# Revit family: Elite_Sliding_Window_XX_Standard
name_source: partatom
category: Windows
revit_build: Autodesk Revit 2014 (Build: 20130308_1515(x64)
units: mm (PartAtom-declared; Revit-internal decimal feet)

## types (108) — shared parameters
Centered In Wall = Yes
Custom Sash Width Left = 600 mm
Default Sill Height = 800 mm
Description = Sliding window, XX
Equal Sash Width = Yes
Frame Thickness = 70 mm
Limit Sash Height Max = 1800 mm  [stored 5.90551 ft]
Limit Sash Height Min = 300 mm
Limit Sash Width Max = 1500 mm  [stored 4.92126 ft]
Limit Sash Width Min = 300 mm
Limit Window Height Max = 1883 mm
Limit Window Height Min = 383 mm  [stored 1.25656 ft]
Limit Window Width Min = 594 mm
Manufacturer = Crealco
Model = Elite
Rough Width = 3 mm  [stored 0.00984252 ft]
Sash Frame Seal = 3 mm  [stored 0.00984252 ft]
Sash Side Spacing = 1 mm  [stored 0.00328084 ft]
URL = http://www.crealco.co.za
Wall Closure = By host
zero-valued in all types: Custom Frame Offset From Exterior

## per-type parameters (varying)
- Elite-0906XX-1000Pa: Area Left Sash Glazing=0.16 m²; Area Right Sash Glazing=0.16 m²; Clearvue SHGC Value=0.456; Clearvue U Value=7.11; Custom Windload=1000 mm  [stored 3.28084 ft]; Custom Window Height=590 mm  [stored 1.9357 ft]; Custom Window Width=890 mm  [stored 2.91995 ft]; Energy Advantage SHGC Value=0.412; Energy Advantage U Value=6.21; Height=590 mm  [stored 1.9357 ft]; Inside Heavy Duty Interlocker=No; Interlocker Configuration=0 mm  [stored 0 ft]; Intruderprufe LowE SHGC Value=0.433; Intruderprufe LowE U Value=6.99; Intruderprufe SHGC Value=0.349; Intruderprufe U Value=7.27; Limit Sash Width Left Max=596 mm; Limit Sash Width Left Min=300 mm; Limit Window Width Max=2994 mm; Max Pane Area=0.16 m²; Outside Heavy Duty Interlocker=No; Sash Height=507 mm; Sash Width Left=448 mm; Sash Width Right=448 mm; Standard Interlocker=Yes; Width=890 mm  [stored 2.91995 ft]; Windload Design=1000 mm  [stored 3.28084 ft]
- Elite-1206XX-1000Pa: Area Left Sash Glazing=0.22 m²; Area Right Sash Glazing=0.22 m²; Clearvue SHGC Value=0.49; Clearvue U Value=7; Custom Windload=1000 mm  [stored 3.28084 ft]; Custom Window Height=590 mm  [stored 1.9357 ft]; Custom Window Width=1190 mm  [stored 3.9042 ft]; Energy Advantage SHGC Value=0.442; Energy Advantage U Value=5.95; Height=590 mm  [stored 1.9357 ft]; Inside Heavy Duty Interlocker=No; Interlocker Configuration=0 mm  [stored 0 ft]; Intruderprufe LowE SHGC Value=0.413; Intruderprufe LowE U Value=5.73; Intruderprufe SHGC Value=0.466; Intruderprufe U Value=6.88; Limit Sash Width Left Max=896 mm; Limit Sash Width Left Min=300 mm; Limit Window Width Max=2994 mm; Max Pane Area=0.22 m²; Outside Heavy Duty Interlocker=No; Sash Height=507 mm; Sash Width Left=598 mm; Sash Width Right=598 mm; Standard Interlocker=Yes; Width=1190 mm  [stored 3.9042 ft]; Windload Design=1000 mm  [stored 3.28084 ft]
- Elite-1506XX-1000Pa: Area Left Sash Glazing=0.28 m²; Area Right Sash Glazing=0.28 m²; Clearvue SHGC Value=0.511; Clearvue U Value=6.93; Custom Windload=1000 mm  [stored 3.28084 ft]; Custom Window Height=590 mm  [stored 1.9357 ft]; Custom Window Width=1490 mm  [stored 4.88845 ft]; Energy Advantage SHGC Value=0.46; Energy Advantage U Value=5.8; Height=590 mm  [stored 1.9357 ft]; Inside Heavy Duty Interlocker=No; Interlocker Configuration=0 mm  [stored 0 ft]; Intruderprufe LowE SHGC Value=0.429; Intruderprufe LowE U Value=5.61; Intruderprufe SHGC Value=0.485; Intruderprufe U Value=6.81; Limit Sash Width Left Max=1196 mm; Limit Sash Width Left Min=300 mm; Limit Window Width Max=2994 mm; Max Pane Area=0.28 m²; Outside Heavy Duty Interlocker=No; Sash Height=507 mm; Sash Width Left=748 mm; Sash Width Right=748 mm; Standard Interlocker=Yes; Width=1490 mm  [stored 4.88845 ft]; Windload Design=1000 mm  [stored 3.28084 ft]
- Elite-1806XX-1000Pa: Area Left Sash Glazing=0.35 m²; Area Right Sash Glazing=0.35 m²; Clearvue SHGC Value=0.524; Clearvue U Value=6.88; Custom Windload=1000 mm  [stored 3.28084 ft]; Custom Window Height=590 mm  [stored 1.9357 ft]; Custom Window Width=1790 mm  [stored 5.8727 ft]; Energy Advantage SHGC Value=0.472; Energy Advantage U Value=5.7; Height=590 mm  [stored 1.9357 ft]; Inside Heavy Duty Interlocker=No; Interlocker Configuration=0 mm  [stored 0 ft]; Intruderprufe LowE SHGC Value=0.44; Intruderprufe LowE U Value=5.52; Intruderprufe SHGC Value=0.498; Intruderprufe U Value=6.76; Limit Sash Width Left Max=1496 mm; Limit Sash Width Left Min=300 mm; Limit Window Width Max=2994 mm; Max Pane Area=0.35 m²; Outside Heavy Duty Interlocker=No; Sash Height=507 mm; Sash Width Left=898 mm; Sash Width Right=898 mm; Standard Interlocker=Yes; Width=1790 mm  [stored 5.8727 ft]; Windload Design=1000 mm  [stored 3.28084 ft]
- Elite-2106XX-1000Pa: Area Left Sash Glazing=0.41 m²; Area Right Sash Glazing=0.41 m²; Clearvue SHGC Value=0.534; Clearvue U Value=6.85; Custom Windload=1000 mm  [stored 3.28084 ft]; Custom Window Height=590 mm  [stored 1.9357 ft]; Custom Window Width=2090 mm  [stored 6.85696 ft]; Energy Advantage SHGC Value=0.48; Energy Advantage U Value=5.63; Height=590 mm  [stored 1.9357 ft]; Inside Heavy Duty Interlocker=No; Interlocker Configuration=0 mm  [stored 0 ft]; Intruderprufe LowE SHGC Value=0.448; Intruderprufe LowE U Value=5.46; Intruderprufe SHGC Value=0.507; Intruderprufe U Value=6.763; Limit Sash Width Left Max=1500 mm  [stored 4.92126 ft]; Limit Sash Width Left Min=596 mm; Limit Window Width Max=2994 mm; Max Pane Area=0.41 m²; Outside Heavy Duty Interlocker=No; Sash Height=507 mm; Sash Width Left=1048 mm; Sash Width Right=1048 mm; Standard Interlocker=Yes; Width=2090 mm  [stored 6.85696 ft]; Windload Design=1000 mm  [stored 3.28084 ft]
- Elite-2406XX-1000Pa: Area Left Sash Glazing=0.47 m²; Area Right Sash Glazing=0.47 m²; Clearvue SHGC Value=0.541; Clearvue U Value=6.82; Custom Windload=1000 mm  [stored 3.28084 ft]; Custom Window Height=590 mm  [stored 1.9357 ft]; Custom Window Width=2390 mm  [stored 7.84121 ft]; Energy Advantage SHGC Value=0.487; Energy Advantage U Value=5.58; Height=590 mm  [stored 1.9357 ft]; Inside Heavy Duty Interlocker=No; Interlocker Configuration=0 mm  [stored 0 ft]; Intruderprufe LowE SHGC Value=0.454; Intruderprufe LowE U Value=5.42; Intruderprufe SHGC Value=0.514; Intruderprufe U Value=6.7; Limit Sash Width Left Max=1500 mm  [stored 4.92126 ft]; Limit Sash Width Left Min=896 mm; Limit Window Width Max=2994 mm; Max Pane Area=0.47 m²; Outside Heavy Duty Interlocker=No; Sash Height=507 mm; Sash Width Left=1198 mm; Sash Width Right=1198 mm; Standard Interlocker=Yes; Width=2390 mm  [stored 7.84121 ft]; Windload Design=1000 mm  [stored 3.28084 ft]
- Elite-2706XX-1000Pa: Area Left Sash Glazing=0.53 m²; Area Right Sash Glazing=0.53 m²; Clearvue SHGC Value=0.547; Clearvue U Value=6.8; Custom Windload=1000 mm  [stored 3.28084 ft]; Custom Window Height=590 mm  [stored 1.9357 ft]; Custom Window Width=2690 mm; Energy Advantage SHGC Value=0.492; Energy Advantage U Value=5.54; Height=590 mm  [stored 1.9357 ft]; Inside Heavy Duty Interlocker=No; Interlocker Configuration=0 mm  [stored 0 ft]; Intruderprufe LowE SHGC Value=0.414; Intruderprufe LowE U Value=6.68; Intruderprufe SHGC Value=0.519; Intruderprufe U Value=6.69; Limit Sash Width Left Max=1500 mm  [stored 4.92126 ft]; Limit Sash Width Left Min=1196 mm; Limit Window Width Max=2994 mm; Max Pane Area=0.53 m²; Outside Heavy Duty Interlocker=No; Sash Height=507 mm; Sash Width Left=1348 mm; Sash Width Right=1348 mm; Standard Interlocker=Yes; Width=2690 mm; Windload Design=1000 mm  [stored 3.28084 ft]
- Elite-3006XX-1000Pa: Area Left Sash Glazing=0.6 m²; Area Right Sash Glazing=0.6 m²; Clearvue SHGC Value=0.551; Clearvue U Value=6.79; Custom Windload=1000 mm  [stored 3.28084 ft]; Custom Window Height=590 mm  [stored 1.9357 ft]; Custom Window Width=2990 mm; Energy Advantage SHGC Value=0.495; Energy Advantage U Value=5.5; Height=590 mm  [stored 1.9357 ft]; Inside Heavy Duty Interlocker=No; Interlocker Configuration=0 mm  [stored 0 ft]; Intruderprufe LowE SHGC Value=0.462; Intruderprufe LowE U Value=5.36; Intruderprufe SHGC Value=0.524; Intruderprufe U Value=6.67; Limit Sash Width Left Max=1500 mm  [stored 4.92126 ft]; Limit Sash Width Left Min=1496 mm; Limit Window Width Max=2994 mm; Max Pane Area=0.6 m²; Outside Heavy Duty Interlocker=No; Sash Height=507 mm; Sash Width Left=1498 mm; Sash Width Right=1498 mm; Standard Interlocker=Yes; Width=2990 mm; Windload Design=1000 mm  [stored 3.28084 ft]
- Elite-0909XX-1000Pa: Area Left Sash Glazing=0.28 m²; Area Right Sash Glazing=0.28 m²; Clearvue SHGC Value=0.521; Clearvue U Value=6.96; Custom Windload=1000 mm  [stored 3.28084 ft]; Custom Window Height=890 mm  [stored 2.91995 ft]; Custom Window Width=890 mm  [stored 2.91995 ft]; Energy Advantage SHGC Value=0.47; Energy Advantage U Value=5.88; Height=890 mm  [stored 2.91995 ft]; Inside Heavy Duty Interlocker=No; Interlocker Configuration=0 mm  [stored 0 ft]; Intruderprufe LowE SHGC Value=0.438; Intruderprufe LowE U Value=5.62; Intruderprufe SHGC Value=0.494; Intruderprufe U Value=6.84; Limit Sash Width Left Max=596 mm; Limit Sash Width Left Min=300 mm; Limit Window Width Max=2994 mm; Max Pane Area=0.28 m²; Outside Heavy Duty Interlocker=No; Sash Height=807 mm  [stored 2.64764 ft]; Sash Width Left=448 mm; Sash Width Right=448 mm; Standard Interlocker=Yes; Width=890 mm  [stored 2.91995 ft]; Windload Design=1000 mm  [stored 3.28084 ft]
- Elite-1209XX-1000Pa: Area Left Sash Glazing=0.38 m²; Area Right Sash Glazing=0.38 m²; Clearvue SHGC Value=0.561; Clearvue U Value=6.82; Custom Windload=1000 mm  [stored 3.28084 ft]; Custom Window Height=890 mm  [stored 2.91995 ft]; Custom Window Width=1190 mm  [stored 3.9042 ft]; Energy Advantage SHGC Value=0.504; Energy Advantage U Value=5.58; Height=890 mm  [stored 2.91995 ft]; Inside Heavy Duty Interlocker=No; Interlocker Configuration=0 mm  [stored 0 ft]; Intruderprufe LowE SHGC Value=0.47; Intruderprufe LowE U Value=5.36; Intruderprufe SHGC Value=0.532; Intruderprufe U Value=6.7; Limit Sash Width Left Max=896 mm; Limit Sash Width Left Min=300 mm; Limit Window Width Max=2994 mm; Max Pane Area=0.38 m²; Outside Heavy Duty Interlocker=No; Sash Height=807 mm  [stored 2.64764 ft]; Sash Width Left=598 mm; Sash Width Right=598 mm; Standard Interlocker=Yes; Width=1190 mm  [stored 3.9042 ft]; Windload Design=1000 mm  [stored 3.28084 ft]
- Elite-1509XX-1000Pa: Area Left Sash Glazing=0.49 m²; Area Right Sash Glazing=0.49 m²; Clearvue SHGC Value=0.584; Clearvue U Value=6.73; Custom Windload=1000 mm  [stored 3.28084 ft]; Custom Window Height=890 mm  [stored 2.91995 ft]; Custom Window Width=1490 mm  [stored 4.88845 ft]; Energy Advantage SHGC Value=0.525; Energy Advantage U Value=5.41; Height=890 mm  [stored 2.91995 ft]; Inside Heavy Duty Interlocker=No; Interlocker Configuration=0 mm  [stored 0 ft]; Intruderprufe LowE SHGC Value=0.489; Intruderprufe LowE U Value=5.21; Intruderprufe SHGC Value=0.55; Intruderprufe U Value=6.61; Limit Sash Width Left Max=1196 mm; Limit Sash Width Left Min=300 mm; Limit Window Width Max=2994 mm; Max Pane Area=0.49 m²; Outside Heavy Duty Interlocker=No; Sash Height=807 mm  [stored 2.64764 ft]; Sash Width Left=748 mm; Sash Width Right=748 mm; Standard Interlocker=Yes; Width=1490 mm  [stored 4.88845 ft]; Windload Design=1000 mm  [stored 3.28084 ft]
- Elite-1809XX-1000Pa: Area Left Sash Glazing=0.6 m²; Area Right Sash Glazing=0.6 m²; Clearvue SHGC Value=2.6; Clearvue U Value=6.68; Custom Windload=1000 mm  [stored 3.28084 ft]; Custom Window Height=890 mm  [stored 2.91995 ft]; Custom Window Width=1790 mm  [stored 5.8727 ft]; Energy Advantage SHGC Value=0.539; Energy Advantage U Value=5.29; Height=890 mm  [stored 2.91995 ft]; Inside Heavy Duty Interlocker=No; Interlocker Configuration=0 mm  [stored 0 ft]; Intruderprufe LowE SHGC Value=0.502; Intruderprufe LowE U Value=5.11; Intruderprufe SHGC Value=0.57; Intruderprufe U Value=6.55; Limit Sash Width Left Max=1496 mm; Limit Sash Width Left Min=300 mm; Limit Window Width Max=2994 mm; Max Pane Area=0.6 m²; Outside Heavy Duty Interlocker=No; Sash Height=807 mm  [stored 2.64764 ft]; Sash Width Left=898 mm; Sash Width Right=898 mm; Standard Interlocker=Yes; Width=1790 mm  [stored 5.8727 ft]; Windload Design=1000 mm  [stored 3.28084 ft]
- Elite-2109XX-1000Pa: Area Left Sash Glazing=0.7 m²; Area Right Sash Glazing=0.7 m²; Clearvue SHGC Value=0.611; Clearvue U Value=6.64; Custom Windload=1000 mm  [stored 3.28084 ft]; Custom Window Height=890 mm  [stored 2.91995 ft]; Custom Window Width=2090 mm  [stored 6.85696 ft]; Energy Advantage SHGC Value=0.549; Energy Advantage U Value=5.2; Height=890 mm  [stored 2.91995 ft]; Inside Heavy Duty Interlocker=No; Interlocker Configuration=0 mm  [stored 0 ft]; Intruderprufe LowE SHGC Value=0.511; Intruderprufe LowE U Value=5.04; Intruderprufe SHGC Value=0.58; Intruderprufe U Value=6.54; Limit Sash Width Left Max=1500 mm  [stored 4.92126 ft]; Limit Sash Width Left Min=596 mm; Limit Window Width Max=2994 mm; Max Pane Area=0.7 m²; Outside Heavy Duty Interlocker=No; Sash Height=807 mm  [stored 2.64764 ft]; Sash Width Left=1048 mm; Sash Width Right=1048 mm; Standard Interlocker=Yes; Width=2090 mm  [stored 6.85696 ft]; Windload Design=1000 mm  [stored 3.28084 ft]
- Elite-2409XX-1000Pa: Area Left Sash Glazing=0.81 m²; Area Right Sash Glazing=0.81 m²; Clearvue SHGC Value=0.62; Clearvue U Value=6.6; Custom Windload=1000 mm  [stored 3.28084 ft]; Custom Window Height=890 mm  [stored 2.91995 ft]; Custom Window Width=2390 mm  [stored 7.84121 ft]; Energy Advantage SHGC Value=0.556; Energy Advantage U Value=5.14; Height=890 mm  [stored 2.91995 ft]; Inside Heavy Duty Interlocker=No; Interlocker Configuration=0 mm  [stored 0 ft]; Intruderprufe LowE SHGC Value=0.518; Intruderprufe LowE U Value=4.99; Intruderprufe SHGC Value=0.588; Intruderprufe U Value=6.48; Limit Sash Width Left Max=1500 mm  [stored 4.92126 ft]; Limit Sash Width Left Min=896 mm; Limit Window Width Max=2994 mm; Max Pane Area=0.81 m²; Outside Heavy Duty Interlocker=No; Sash Height=807 mm  [stored 2.64764 ft]; Sash Width Left=1198 mm; Sash Width Right=1198 mm; Standard Interlocker=Yes; Width=2390 mm  [stored 7.84121 ft]; Windload Design=1000 mm  [stored 3.28084 ft]
- Elite-2709XX-1000Pa: Area Left Sash Glazing=0.92 m²; Area Right Sash Glazing=0.92 m²; Clearvue SHGC Value=0.626; Clearvue U Value=6.58; Custom Windload=1000 mm  [stored 3.28084 ft]; Custom Window Height=890 mm  [stored 2.91995 ft]; Custom Window Width=2690 mm; Energy Advantage SHGC Value=0.562; Energy Advantage U Value=5.09; Height=890 mm  [stored 2.91995 ft]; Inside Heavy Duty Interlocker=No; Interlocker Configuration=0 mm  [stored 0 ft]; Intruderprufe LowE SHGC Value=0.523; Intruderprufe LowE U Value=4.94; Intruderprufe SHGC Value=0.595; Intruderprufe U Value=6.46; Limit Sash Width Left Max=1500 mm  [stored 4.92126 ft]; Limit Sash Width Left Min=1196 mm; Limit Window Width Max=2994 mm; Max Pane Area=0.92 m²; Outside Heavy Duty Interlocker=No; Sash Height=807 mm  [stored 2.64764 ft]; Sash Width Left=1348 mm; Sash Width Right=1348 mm; Standard Interlocker=Yes; Width=2690 mm; Windload Design=1000 mm  [stored 3.28084 ft]
- Elite-3009XX-1000Pa: Area Left Sash Glazing=1.03 m²; Area Right Sash Glazing=1.03 m²; Clearvue SHGC Value=0.632; Clearvue U Value=6.56; Custom Windload=1000 mm  [stored 3.28084 ft]; Custom Window Height=890 mm  [stored 2.91995 ft]; Custom Window Width=2990 mm; Energy Advantage SHGC Value=0.567; Energy Advantage U Value=5.05; Height=890 mm  [stored 2.91995 ft]; Inside Heavy Duty Interlocker=No; Interlocker Configuration=0 mm  [stored 0 ft]; Intruderprufe LowE SHGC Value=0.528; Intruderprufe LowE U Value=4.91; Intruderprufe SHGC Value=0.6; Intruderprufe U Value=6.44; Limit Sash Width Left Max=1500 mm  [stored 4.92126 ft]; Limit Sash Width Left Min=1496 mm; Limit Window Width Max=2994 mm; Max Pane Area=1.03 m²; Outside Heavy Duty Interlocker=No; Sash Height=807 mm  [stored 2.64764 ft]; Sash Width Left=1498 mm; Sash Width Right=1498 mm; Standard Interlocker=Yes; Width=2990 mm; Windload Design=1000 mm  [stored 3.28084 ft]
- Elite-0912XX-1000Pa: Area Left Sash Glazing=0.39 m²; Area Right Sash Glazing=0.39 m²; Clearvue SHGC Value=0.553; Clearvue U Value=6.89; Custom Windload=1000 mm  [stored 3.28084 ft]; Custom Window Height=1190 mm  [stored 3.9042 ft]; Custom Window Width=890 mm  [stored 2.91995 ft]; Energy Advantage SHGC Value=0.4798; Energy Advantage U Value=5.72; Height=1190 mm  [stored 3.9042 ft]; Inside Heavy Duty Interlocker=No; Interlocker Configuration=0 mm  [stored 0 ft]; Intruderprufe LowE SHGC Value=0.464; Intruderprufe LowE U Value=5.35; Intruderprufe SHGC Value=0.525; Intruderprufe U Value=6.76; Limit Sash Width Left Max=596 mm; Limit Sash Width Left Min=300 mm; Limit Window Width Max=2994 mm; Max Pane Area=0.39 m²; Outside Heavy Duty Interlocker=No; Sash Height=1107 mm  [stored 3.63189 ft]; Sash Width Left=448 mm; Sash Width Right=448 mm; Standard Interlocker=Yes; Width=890 mm  [stored 2.91995 ft]; Windload Design=1000 mm  [stored 3.28084 ft]
- Elite-1212XX-1000Pa: Area Left Sash Glazing=0.54 m²; Area Right Sash Glazing=0.54 m²; Clearvue SHGC Value=0.595; Clearvue U Value=6.73; Custom Windload=1000 mm  [stored 3.28084 ft]; Custom Window Height=1190 mm  [stored 3.9042 ft]; Custom Window Width=1190 mm  [stored 3.9042 ft]; Energy Advantage SHGC Value=0.535; Energy Advantage U Value=5.4; Height=1190 mm  [stored 3.9042 ft]; Inside Heavy Duty Interlocker=No; Interlocker Configuration=0 mm  [stored 0 ft]; Intruderprufe LowE SHGC Value=0.498; Intruderprufe LowE U Value=5.18; Intruderprufe SHGC Value=0.565; Intruderprufe U Value=6.61; Limit Sash Width Left Max=896 mm; Limit Sash Width Left Min=300 mm; Limit Window Width Max=2994 mm; Max Pane Area=0.54 m²; Outside Heavy Duty Interlocker=No; Sash Height=1107 mm  [stored 3.63189 ft]; Sash Width Left=598 mm; Sash Width Right=598 mm; Standard Interlocker=Yes; Width=1190 mm  [stored 3.9042 ft]; Windload Design=1000 mm  [stored 3.28084 ft]
- Elite-1512XX-1000Pa: Area Left Sash Glazing=0.7 m²; Area Right Sash Glazing=0.7 m²; Clearvue SHGC Value=0.621; Clearvue U Value=6.64; Custom Windload=1000 mm  [stored 3.28084 ft]; Custom Window Height=1190 mm  [stored 3.9042 ft]; Custom Window Width=1490 mm  [stored 4.88845 ft]; Energy Advantage SHGC Value=0.558; Energy Advantage U Value=5.21; Height=1190 mm  [stored 3.9042 ft]; Inside Heavy Duty Interlocker=No; Interlocker Configuration=0 mm  [stored 0 ft]; Intruderprufe LowE SHGC Value=0.519; Intruderprufe LowE U Value=5.01; Intruderprufe SHGC Value=0.589; Intruderprufe U Value=6.51; Limit Sash Width Left Max=1196 mm; Limit Sash Width Left Min=300 mm; Limit Window Width Max=2994 mm; Max Pane Area=0.7 m²; Outside Heavy Duty Interlocker=No; Sash Height=1107 mm  [stored 3.63189 ft]; Sash Width Left=748 mm; Sash Width Right=748 mm; Standard Interlocker=Yes; Width=1490 mm  [stored 4.88845 ft]; Windload Design=1000 mm  [stored 3.28084 ft]
- Elite-1812XX-1000Pa: Area Left Sash Glazing=0.85 m²; Area Right Sash Glazing=0.85 m²; Clearvue SHGC Value=0.638; Clearvue U Value=6.57; Custom Windload=1000 mm  [stored 3.28084 ft]; Custom Window Height=1190 mm  [stored 3.9042 ft]; Custom Window Width=1790 mm  [stored 5.8727 ft]; Energy Advantage SHGC Value=0.572; Energy Advantage U Value=5.08; Height=1190 mm  [stored 3.9042 ft]; Inside Heavy Duty Interlocker=No; Interlocker Configuration=0 mm  [stored 0 ft]; Intruderprufe LowE SHGC Value=0.533; Intruderprufe LowE U Value=4.91; Intruderprufe SHGC Value=0.605; Intruderprufe U Value=6.45; Limit Sash Width Left Max=1496 mm; Limit Sash Width Left Min=300 mm; Limit Window Width Max=2994 mm; Max Pane Area=0.85 m²; Outside Heavy Duty Interlocker=No; Sash Height=1107 mm  [stored 3.63189 ft]; Sash Width Left=898 mm; Sash Width Right=898 mm; Standard Interlocker=Yes; Width=1790 mm  [stored 5.8727 ft]; Windload Design=1000 mm  [stored 3.28084 ft]
- Elite-2112XX-1000Pa: Area Left Sash Glazing=1 m²; Area Right Sash Glazing=1 m²; Clearvue SHGC Value=0.65; Clearvue U Value=6.53; Custom Windload=1000 mm  [stored 3.28084 ft]; Custom Window Height=1190 mm  [stored 3.9042 ft]; Custom Window Width=2090 mm  [stored 6.85696 ft]; Energy Advantage SHGC Value=0.583; Energy Advantage U Value=4.99; Height=1190 mm  [stored 3.9042 ft]; Inside Heavy Duty Interlocker=No; Interlocker Configuration=0 mm  [stored 0 ft]; Intruderprufe LowE SHGC Value=0.542; Intruderprufe LowE U Value=4.83; Intruderprufe SHGC Value=0.617; Intruderprufe U Value=6.4; Limit Sash Width Left Max=1500 mm  [stored 4.92126 ft]; Limit Sash Width Left Min=596 mm; Limit Window Width Max=2994 mm; Max Pane Area=1 m²; Outside Heavy Duty Interlocker=No; Sash Height=1107 mm  [stored 3.63189 ft]; Sash Width Left=1048 mm; Sash Width Right=1048 mm; Standard Interlocker=Yes; Width=2090 mm  [stored 6.85696 ft]; Windload Design=1000 mm  [stored 3.28084 ft]
- Elite-2412XX-1000Pa: Area Left Sash Glazing=1.15 m²; Area Right Sash Glazing=1.15 m²; Clearvue SHGC Value=0.659; Clearvue U Value=6.5; Custom Windload=1000 mm  [stored 3.28084 ft]; Custom Window Height=1190 mm  [stored 3.9042 ft]; Custom Window Width=2390 mm  [stored 7.84121 ft]; Energy Advantage SHGC Value=0.591; Energy Advantage U Value=4.92; Height=1190 mm  [stored 3.9042 ft]; Inside Heavy Duty Interlocker=No; Interlocker Configuration=0 mm  [stored 0 ft]; Intruderprufe LowE SHGC Value=0.55; Intruderprufe LowE U Value=4.77; Intruderprufe SHGC Value=0.625; Intruderprufe U Value=6.37; Limit Sash Width Left Max=1500 mm  [stored 4.92126 ft]; Limit Sash Width Left Min=896 mm; Limit Window Width Max=2994 mm; Max Pane Area=1.15 m²; Outside Heavy Duty Interlocker=No; Sash Height=1107 mm  [stored 3.63189 ft]; Sash Width Left=1198 mm; Sash Width Right=1198 mm; Standard Interlocker=Yes; Width=2390 mm  [stored 7.84121 ft]; Windload Design=1000 mm  [stored 3.28084 ft]
- Elite-2712XX-1000Pa: Area Left Sash Glazing=1.31 m²; Area Right Sash Glazing=1.31 m²; Clearvue SHGC Value=0.666; Clearvue U Value=6.47; Custom Windload=1000 mm  [stored 3.28084 ft]; Custom Window Height=1190 mm  [stored 3.9042 ft]; Custom Window Width=2690 mm; Energy Advantage SHGC Value=0.597; Energy Advantage U Value=4.87; Height=1190 mm  [stored 3.9042 ft]; Inside Heavy Duty Interlocker=No; Interlocker Configuration=0 mm  [stored 0 ft]; Intruderprufe LowE SHGC Value=0.556; Intruderprufe LowE U Value=4.72; Intruderprufe SHGC Value=0.632; Intruderprufe U Value=6.35; Limit Sash Width Left Max=1500 mm  [stored 4.92126 ft]; Limit Sash Width Left Min=1196 mm; Limit Window Width Max=2994 mm; Max Pane Area=1.31 m²; Outside Heavy Duty Interlocker=No; Sash Height=1107 mm  [stored 3.63189 ft]; Sash Width Left=1348 mm; Sash Width Right=1348 mm; Standard Interlocker=Yes; Width=2690 mm; Windload Design=1000 mm  [stored 3.28084 ft]
- Elite-3012XX-1000Pa: Area Left Sash Glazing=1.46 m²; Area Right Sash Glazing=1.46 m²; Clearvue SHGC Value=0.672; Clearvue U Value=6.45; Custom Windload=1000 mm  [stored 3.28084 ft]; Custom Window Height=1190 mm  [stored 3.9042 ft]; Custom Window Width=2990 mm; Energy Advantage SHGC Value=0.602; Energy Advantage U Value=4.83; Height=1190 mm  [stored 3.9042 ft]; Inside Heavy Duty Interlocker=Yes; Interlocker Configuration=1 mm  [stored 0.00328084 ft]; Intruderprufe LowE SHGC Value=0.56; Intruderprufe LowE U Value=4.69; Intruderprufe SHGC Value=0.637; Intruderprufe U Value=6.32; Limit Sash Width Left Max=1500 mm  [stored 4.92126 ft]; Limit Sash Width Left Min=1496 mm; Limit Window Width Max=2994 mm; Max Pane Area=1.46 m²; Outside Heavy Duty Interlocker=No; Sash Height=1107 mm  [stored 3.63189 ft]; Sash Width Left=1498 mm; Sash Width Right=1498 mm; Standard Interlocker=No; Width=2990 mm; Windload Design=1000 mm  [stored 3.28084 ft]
- Elite-0915XX-1000Pa: Area Left Sash Glazing=0.51 m²; Area Right Sash Glazing=0.51 m²; Clearvue SHGC Value=0.572; Clearvue U Value=6.85; Custom Windload=1000 mm  [stored 3.28084 ft]; Custom Window Height=1490 mm  [stored 4.88845 ft]; Custom Window Width=890 mm  [stored 2.91995 ft]; Energy Advantage SHGC Value=0.515; Energy Advantage U Value=5.62; Height=1490 mm  [stored 4.88845 ft]; Inside Heavy Duty Interlocker=No; Interlocker Configuration=0 mm  [stored 0 ft]; Intruderprufe LowE SHGC Value=0.479; Intruderprufe LowE U Value=5.36; Intruderprufe SHGC Value=0.543; Intruderprufe U Value=6.72; Limit Sash Width Left Max=596 mm; Limit Sash Width Left Min=300 mm; Limit Window Width Max=2994 mm; Max Pane Area=0.51 m²; Outside Heavy Duty Interlocker=No; Sash Height=1407 mm  [stored 4.61614 ft]; Sash Width Left=448 mm; Sash Width Right=448 mm; Standard Interlocker=Yes; Width=890 mm  [stored 2.91995 ft]; Windload Design=1000 mm  [stored 3.28084 ft]
- Elite-1215XX-1000Pa: Area Left Sash Glazing=0.7 m²; Area Right Sash Glazing=0.7 m²; Clearvue SHGC Value=0.616; Clearvue U Value=6.68; Custom Windload=1000 mm  [stored 3.28084 ft]; Custom Window Height=1490 mm  [stored 4.88845 ft]; Custom Window Width=1190 mm  [stored 3.9042 ft]; Energy Advantage SHGC Value=0.554; Energy Advantage U Value=5.29; Height=1490 mm  [stored 4.88845 ft]; Inside Heavy Duty Interlocker=Yes; Interlocker Configuration=1 mm  [stored 0.00328084 ft]; Intruderprufe LowE SHGC Value=0.515; Intruderprufe LowE U Value=5.07; Intruderprufe SHGC Value=0.585; Intruderprufe U Value=6.55; Limit Sash Width Left Max=896 mm; Limit Sash Width Left Min=300 mm; Limit Window Width Max=2994 mm; Max Pane Area=0.7 m²; Outside Heavy Duty Interlocker=No; Sash Height=1407 mm  [stored 4.61614 ft]; Sash Width Left=598 mm; Sash Width Right=598 mm; Standard Interlocker=No; Width=1190 mm  [stored 3.9042 ft]; Windload Design=1000 mm  [stored 3.28084 ft]
- Elite-1515XX-1000Pa: Area Left Sash Glazing=0.9 m²; Area Right Sash Glazing=0.9 m²; Clearvue SHGC Value=0.643; Clearvue U Value=6.58; Custom Windload=1000 mm  [stored 3.28084 ft]; Custom Window Height=1490 mm  [stored 4.88845 ft]; Custom Window Width=1490 mm  [stored 4.88845 ft]; Energy Advantage SHGC Value=0.577; Energy Advantage U Value=5.09; Height=1490 mm  [stored 4.88845 ft]; Inside Heavy Duty Interlocker=Yes; Interlocker Configuration=1 mm  [stored 0.00328084 ft]; Intruderprufe LowE SHGC Value=0.537; Intruderprufe LowE U Value=4.9; Intruderprufe SHGC Value=0.61; Intruderprufe U Value=6.45; Limit Sash Width Left Max=1196 mm; Limit Sash Width Left Min=300 mm; Limit Window Width Max=2994 mm; Max Pane Area=0.9 m²; Outside Heavy Duty Interlocker=No; Sash Height=1407 mm  [stored 4.61614 ft]; Sash Width Left=748 mm; Sash Width Right=748 mm; Standard Interlocker=No; Width=1490 mm  [stored 4.88845 ft]; Windload Design=1000 mm  [stored 3.28084 ft]
- Elite-1815XX-1000Pa: Area Left Sash Glazing=1.1 m²; Area Right Sash Glazing=1.1 m²; Clearvue SHGC Value=0.66; Clearvue U Value=6.51; Custom Windload=1000 mm  [stored 3.28084 ft]; Custom Window Height=1490 mm  [stored 4.88845 ft]; Custom Window Width=1790 mm  [stored 5.8727 ft]; Energy Advantage SHGC Value=0.592; Energy Advantage U Value=4.96; Height=1490 mm  [stored 4.88845 ft]; Inside Heavy Duty Interlocker=Yes; Interlocker Configuration=1 mm  [stored 0.00328084 ft]; Intruderprufe LowE SHGC Value=0.551; Intruderprufe LowE U Value=4.78; Intruderprufe SHGC Value=0.627; Intruderprufe U Value=6.39; Limit Sash Width Left Max=1496 mm; Limit Sash Width Left Min=300 mm; Limit Window Width Max=2994 mm; Max Pane Area=1.1 m²; Outside Heavy Duty Interlocker=No; Sash Height=1407 mm  [stored 4.61614 ft]; Sash Width Left=898 mm; Sash Width Right=898 mm; Standard Interlocker=No; Width=1790 mm  [stored 5.8727 ft]; Windload Design=1000 mm  [stored 3.28084 ft]
- Elite-2115XX-1000Pa: Area Left Sash Glazing=1.3 m²; Area Right Sash Glazing=1.3 m²; Clearvue SHGC Value=0.673; Clearvue U Value=6.47; Custom Windload=1000 mm  [stored 3.28084 ft]; Custom Window Height=1490 mm  [stored 4.88845 ft]; Custom Window Width=2090 mm  [stored 6.85696 ft]; Energy Advantage SHGC Value=0.603; Energy Advantage U Value=4.86; Height=1490 mm  [stored 4.88845 ft]; Inside Heavy Duty Interlocker=Yes; Interlocker Configuration=1 mm  [stored 0.00328084 ft]; Intruderprufe LowE SHGC Value=0.561; Intruderprufe LowE U Value=4.7; Intruderprufe SHGC Value=0.638; Intruderprufe U Value=6.34; Limit Sash Width Left Max=1500 mm  [stored 4.92126 ft]; Limit Sash Width Left Min=596 mm; Limit Window Width Max=2994 mm; Max Pane Area=1.3 m²; Outside Heavy Duty Interlocker=No; Sash Height=1407 mm  [stored 4.61614 ft]; Sash Width Left=1048 mm; Sash Width Right=1048 mm; Standard Interlocker=No; Width=2090 mm  [stored 6.85696 ft]; Windload Design=1000 mm  [stored 3.28084 ft]
- Elite-2415XX-1000Pa: Area Left Sash Glazing=1.49 m²; Area Right Sash Glazing=1.49 m²; Clearvue SHGC Value=0.682; Clearvue U Value=6.43; Custom Windload=1000 mm  [stored 3.28084 ft]; Custom Window Height=1490 mm  [stored 4.88845 ft]; Custom Window Width=2390 mm  [stored 7.84121 ft]; Energy Advantage SHGC Value=0.611; Energy Advantage U Value=4.79; Height=1490 mm  [stored 4.88845 ft]; Inside Heavy Duty Interlocker=Yes; Interlocker Configuration=1 mm  [stored 0.00328084 ft]; Intruderprufe LowE SHGC Value=0.569; Intruderprufe LowE U Value=4.64; Intruderprufe SHGC Value=0.647; Intruderprufe U Value=6.31; Limit Sash Width Left Max=1500 mm  [stored 4.92126 ft]; Limit Sash Width Left Min=896 mm; Limit Window Width Max=2994 mm; Max Pane Area=1.49 m²; Outside Heavy Duty Interlocker=No; Sash Height=1407 mm  [stored 4.61614 ft]; Sash Width Left=1198 mm; Sash Width Right=1198 mm; Standard Interlocker=No; Width=2390 mm  [stored 7.84121 ft]; Windload Design=1000 mm  [stored 3.28084 ft]
- Elite-2715XX-1000Pa: Area Left Sash Glazing=1.69 m²; Area Right Sash Glazing=1.69 m²; Clearvue SHGC Value=0.69; Clearvue U Value=6.4; Custom Windload=1000 mm  [stored 3.28084 ft]; Custom Window Height=1490 mm  [stored 4.88845 ft]; Custom Window Width=2690 mm; Energy Advantage SHGC Value=0.618; Energy Advantage U Value=4.74; Height=1490 mm  [stored 4.88845 ft]; Inside Heavy Duty Interlocker=Yes; Interlocker Configuration=1 mm  [stored 0.00328084 ft]; Intruderprufe LowE SHGC Value=0.575; Intruderprufe LowE U Value=4.59; Intruderprufe SHGC Value=0.654; Intruderprufe U Value=6.28; Limit Sash Width Left Max=1500 mm  [stored 4.92126 ft]; Limit Sash Width Left Min=1196 mm; Limit Window Width Max=2994 mm; Max Pane Area=1.69 m²; Outside Heavy Duty Interlocker=No; Sash Height=1407 mm  [stored 4.61614 ft]; Sash Width Left=1348 mm; Sash Width Right=1348 mm; Standard Interlocker=No; Width=2690 mm; Windload Design=1000 mm  [stored 3.28084 ft]
- Elite-3015XX-1000Pa: Area Left Sash Glazing=1.89 m²; Area Right Sash Glazing=1.89 m²; Clearvue SHGC Value=0.695; Clearvue U Value=6.38; Custom Windload=1000 mm  [stored 3.28084 ft]; Custom Window Height=1490 mm  [stored 4.88845 ft]; Custom Window Width=2990 mm; Energy Advantage SHGC Value=0.623; Energy Advantage U Value=4.69; Height=1490 mm  [stored 4.88845 ft]; Inside Heavy Duty Interlocker=Yes; Interlocker Configuration=1 mm  [stored 0.00328084 ft]; Intruderprufe LowE SHGC Value=0.579; Intruderprufe LowE U Value=4.56; Intruderprufe SHGC Value=0.66; Intruderprufe U Value=6.26; Limit Sash Width Left Max=1500 mm  [stored 4.92126 ft]; Limit Sash Width Left Min=1496 mm; Limit Window Width Max=2994 mm; Max Pane Area=1.89 m²; Outside Heavy Duty Interlocker=No; Sash Height=1407 mm  [stored 4.61614 ft]; Sash Width Left=1498 mm; Sash Width Right=1498 mm; Standard Interlocker=No; Width=2990 mm; Windload Design=1000 mm  [stored 3.28084 ft]
- Elite-0918XX-1000Pa: Area Left Sash Glazing=0.62 m²; Area Right Sash Glazing=0.62 m²; Clearvue SHGC Value=0.585; Clearvue U Value=6.82; Custom Windload=1000 mm  [stored 3.28084 ft]; Custom Window Height=1790 mm  [stored 5.8727 ft]; Custom Window Width=890 mm  [stored 2.91995 ft]; Energy Advantage SHGC Value=0.526; Energy Advantage U Value=5.56; Height=1790 mm  [stored 5.8727 ft]; Inside Heavy Duty Interlocker=Yes; Interlocker Configuration=1 mm  [stored 0.00328084 ft]; Intruderprufe LowE SHGC Value=0.489; Intruderprufe LowE U Value=5.29; Intruderprufe SHGC Value=0.555; Intruderprufe U Value=6.69; Limit Sash Width Left Max=596 mm; Limit Sash Width Left Min=300 mm; Limit Window Width Max=2994 mm; Max Pane Area=0.62 m²; Outside Heavy Duty Interlocker=No; Sash Height=1707 mm; Sash Width Left=448 mm; Sash Width Right=448 mm; Standard Interlocker=No; Width=890 mm  [stored 2.91995 ft]; Windload Design=1000 mm  [stored 3.28084 ft]
- Elite-1218XX-1000Pa: Area Left Sash Glazing=0.87 m²; Area Right Sash Glazing=0.87 m²; Clearvue SHGC Value=0.63; Clearvue U Value=6.64; Custom Windload=1000 mm  [stored 3.28084 ft]; Custom Window Height=1790 mm  [stored 5.8727 ft]; Custom Window Width=1190 mm  [stored 3.9042 ft]; Energy Advantage SHGC Value=0.566; Energy Advantage U Value=5.22; Height=1790 mm  [stored 5.8727 ft]; Inside Heavy Duty Interlocker=Yes; Interlocker Configuration=1 mm  [stored 0.00328084 ft]; Intruderprufe LowE SHGC Value=0.526; Intruderprufe LowE U Value=5; Intruderprufe SHGC Value=0.598; Intruderprufe U Value=6.52; Limit Sash Width Left Max=896 mm; Limit Sash Width Left Min=300 mm; Limit Window Width Max=2994 mm; Max Pane Area=0.87 m²; Outside Heavy Duty Interlocker=No; Sash Height=1707 mm; Sash Width Left=598 mm; Sash Width Right=598 mm; Standard Interlocker=No; Width=1190 mm  [stored 3.9042 ft]; Windload Design=1000 mm  [stored 3.28084 ft]
- Elite-1518XX-1000Pa: Area Left Sash Glazing=1.11 m²; Area Right Sash Glazing=1.11 m²; Clearvue SHGC Value=0.657; Clearvue U Value=6.54; Custom Windload=1000 mm  [stored 3.28084 ft]; Custom Window Height=1790 mm  [stored 5.8727 ft]; Custom Window Width=1490 mm  [stored 4.88845 ft]; Energy Advantage SHGC Value=0.59; Energy Advantage U Value=5.01; Height=1790 mm  [stored 5.8727 ft]; Inside Heavy Duty Interlocker=Yes; Interlocker Configuration=2 mm  [stored 0.00656168 ft]; Intruderprufe LowE SHGC Value=0.548; Intruderprufe LowE U Value=4.82; Intruderprufe SHGC Value=0.624; Intruderprufe U Value=6.41; Limit Sash Width Left Max=1196 mm; Limit Sash Width Left Min=300 mm; Limit Window Width Max=2994 mm; Max Pane Area=1.11 m²; Outside Heavy Duty Interlocker=Yes; Sash Height=1707 mm; Sash Width Left=748 mm; Sash Width Right=748 mm; Standard Interlocker=No; Width=1490 mm  [stored 4.88845 ft]; Windload Design=1000 mm  [stored 3.28084 ft]
- Elite-1818XX-1000Pa: Area Left Sash Glazing=1.35 m²; Area Right Sash Glazing=1.35 m²; Clearvue SHGC Value=0.675; Clearvue U Value=6.47; Custom Windload=1000 mm  [stored 3.28084 ft]; Custom Window Height=1790 mm  [stored 5.8727 ft]; Custom Window Width=1790 mm  [stored 5.8727 ft]; Energy Advantage SHGC Value=0.605; Energy Advantage U Value=4.88; Height=1790 mm  [stored 5.8727 ft]; Inside Heavy Duty Interlocker=Yes; Interlocker Configuration=2 mm  [stored 0.00656168 ft]; Intruderprufe LowE SHGC Value=0.563; Intruderprufe LowE U Value=4.7; Intruderprufe SHGC Value=0.641; Intruderprufe U Value=6.35; Limit Sash Width Left Max=1496 mm; Limit Sash Width Left Min=300 mm; Limit Window Width Max=2994 mm; Max Pane Area=1.35 m²; Outside Heavy Duty Interlocker=Yes; Sash Height=1707 mm; Sash Width Left=898 mm; Sash Width Right=898 mm; Standard Interlocker=No; Width=1790 mm  [stored 5.8727 ft]; Windload Design=1000 mm  [stored 3.28084 ft]
- Elite-2118XX-1000Pa: Area Left Sash Glazing=1.59 m²; Area Right Sash Glazing=1.59 m²; Clearvue SHGC Value=0.688; Clearvue U Value=6.42; Custom Windload=1000 mm  [stored 3.28084 ft]; Custom Window Height=1790 mm  [stored 5.8727 ft]; Custom Window Width=2090 mm  [stored 6.85696 ft]; Energy Advantage SHGC Value=0.617; Energy Advantage U Value=4.78; Height=1790 mm  [stored 5.8727 ft]; Inside Heavy Duty Interlocker=Yes; Interlocker Configuration=2 mm  [stored 0.00656168 ft]; Intruderprufe LowE SHGC Value=0.574; Intruderprufe LowE U Value=4.62; Intruderprufe SHGC Value=0.653; Intruderprufe U Value=6.3; Limit Sash Width Left Max=1500 mm  [stored 4.92126 ft]; Limit Sash Width Left Min=596 mm; Limit Window Width Max=2994 mm; Max Pane Area=1.59 m²; Outside Heavy Duty Interlocker=Yes; Sash Height=1707 mm; Sash Width Left=1048 mm; Sash Width Right=1048 mm; Standard Interlocker=No; Width=2090 mm  [stored 6.85696 ft]; Windload Design=1000 mm  [stored 3.28084 ft]
- Elite-2418XX-1000Pa: Area Left Sash Glazing=1.83 m²; Area Right Sash Glazing=1.83 m²; Clearvue SHGC Value=0.698; Clearvue U Value=6.39; Custom Windload=1000 mm  [stored 3.28084 ft]; Custom Window Height=1790 mm  [stored 5.8727 ft]; Custom Window Width=2390 mm  [stored 7.84121 ft]; Energy Advantage SHGC Value=0.625; Energy Advantage U Value=4.71; Height=1790 mm  [stored 5.8727 ft]; Inside Heavy Duty Interlocker=Yes; Interlocker Configuration=2 mm  [stored 0.00656168 ft]; Intruderprufe LowE SHGC Value=0.581; Intruderprufe LowE U Value=4.56; Intruderprufe SHGC Value=0.662; Intruderprufe U Value=6.26; Limit Sash Width Left Max=1500 mm  [stored 4.92126 ft]; Limit Sash Width Left Min=896 mm; Limit Window Width Max=2994 mm; Max Pane Area=1.83 m²; Outside Heavy Duty Interlocker=Yes; Sash Height=1707 mm; Sash Width Left=1198 mm; Sash Width Right=1198 mm; Standard Interlocker=No; Width=2390 mm  [stored 7.84121 ft]; Windload Design=1000 mm  [stored 3.28084 ft]
- Elite-2718XX-1000Pa: Area Left Sash Glazing=2.08 m²; Area Right Sash Glazing=2.08 m²; Clearvue SHGC Value=0.705; Clearvue U Value=6.36; Custom Windload=1000 mm  [stored 3.28084 ft]; Custom Window Height=1790 mm  [stored 5.8727 ft]; Custom Window Width=2690 mm; Energy Advantage SHGC Value=0.632; Energy Advantage U Value=4.65; Height=1790 mm  [stored 5.8727 ft]; Inside Heavy Duty Interlocker=Yes; Interlocker Configuration=2 mm  [stored 0.00656168 ft]; Intruderprufe LowE SHGC Value=0.587; Intruderprufe LowE U Value=4.51; Intruderprufe SHGC Value=0.669; Intruderprufe U Value=6.23; Limit Sash Width Left Max=1500 mm  [stored 4.92126 ft]; Limit Sash Width Left Min=1196 mm; Limit Window Width Max=2994 mm; Max Pane Area=2.08 m²; Outside Heavy Duty Interlocker=Yes; Sash Height=1707 mm; Sash Width Left=1348 mm; Sash Width Right=1348 mm; Standard Interlocker=No; Width=2690 mm; Windload Design=1000 mm  [stored 3.28084 ft]
- Elite-3018XX-1000Pa: Area Left Sash Glazing=2.32 m²; Area Right Sash Glazing=2.32 m²; Clearvue SHGC Value=0.711; Clearvue U Value=6.34; Custom Windload=1000 mm  [stored 3.28084 ft]; Custom Window Height=1790 mm  [stored 5.8727 ft]; Custom Window Width=2990 mm; Energy Advantage SHGC Value=0.637; Energy Advantage U Value=4.6; Height=1790 mm  [stored 5.8727 ft]; Inside Heavy Duty Interlocker=Yes; Interlocker Configuration=2 mm  [stored 0.00656168 ft]; Intruderprufe LowE SHGC Value=0.592; Intruderprufe LowE U Value=4.47; Intruderprufe SHGC Value=0.675; Intruderprufe U Value=6.21; Limit Sash Width Left Max=1500 mm  [stored 4.92126 ft]; Limit Sash Width Left Min=1496 mm; Limit Window Width Max=2994 mm; Max Pane Area=2.32 m²; Outside Heavy Duty Interlocker=Yes; Sash Height=1707 mm; Sash Width Left=1498 mm; Sash Width Right=1498 mm; Standard Interlocker=No; Width=2990 mm; Windload Design=1000 mm  [stored 3.28084 ft]
- Elite-0906XX-1500Pa: Area Left Sash Glazing=0.16 m²; Area Right Sash Glazing=0.16 m²; Clearvue SHGC Value=0.456; Clearvue U Value=7.11; Custom Windload=1500 mm  [stored 4.92126 ft]; Custom Window Height=590 mm  [stored 1.9357 ft]; Custom Window Width=890 mm  [stored 2.91995 ft]; Energy Advantage SHGC Value=0.412; Energy Advantage U Value=6.21; Height=590 mm  [stored 1.9357 ft]; Inside Heavy Duty Interlocker=No; Interlocker Configuration=0 mm  [stored 0 ft]; Intruderprufe LowE SHGC Value=0.433; Intruderprufe LowE U Value=6.99; Intruderprufe SHGC Value=0.349; Intruderprufe U Value=7.27; Limit Sash Width Left Max=596 mm; Limit Sash Width Left Min=300 mm; Limit Window Width Max=2994 mm; Max Pane Area=0.16 m²; Outside Heavy Duty Interlocker=No; Sash Height=507 mm; Sash Width Left=448 mm; Sash Width Right=448 mm; Standard Interlocker=Yes; Width=890 mm  [stored 2.91995 ft]; Windload Design=1500 mm  [stored 4.92126 ft]
- Elite-0906XX-2000Pa: Area Left Sash Glazing=0.16 m²; Area Right Sash Glazing=0.16 m²; Clearvue SHGC Value=0.456; Clearvue U Value=7.11; Custom Windload=2000 mm  [stored 6.56168 ft]; Custom Window Height=590 mm  [stored 1.9357 ft]; Custom Window Width=890 mm  [stored 2.91995 ft]; Energy Advantage SHGC Value=0.412; Energy Advantage U Value=6.21; Height=590 mm  [stored 1.9357 ft]; Inside Heavy Duty Interlocker=No; Interlocker Configuration=0 mm  [stored 0 ft]; Intruderprufe LowE SHGC Value=0.433; Intruderprufe LowE U Value=6.99; Intruderprufe SHGC Value=0.349; Intruderprufe U Value=7.27; Limit Sash Width Left Max=596 mm; Limit Sash Width Left Min=300 mm; Limit Window Width Max=2994 mm; Max Pane Area=0.16 m²; Outside Heavy Duty Interlocker=No; Sash Height=507 mm; Sash Width Left=448 mm; Sash Width Right=448 mm; Standard Interlocker=Yes; Width=890 mm  [stored 2.91995 ft]; Windload Design=2000 mm  [stored 6.56168 ft]
- Elite-0909XX-1500Pa: Area Left Sash Glazing=0.28 m²; Area Right Sash Glazing=0.28 m²; Clearvue SHGC Value=0.521; Clearvue U Value=6.96; Custom Windload=1500 mm  [stored 4.92126 ft]; Custom Window Height=890 mm  [stored 2.91995 ft]; Custom Window Width=890 mm  [stored 2.91995 ft]; Energy Advantage SHGC Value=0.47; Energy Advantage U Value=5.88; Height=890 mm  [stored 2.91995 ft]; Inside Heavy Duty Interlocker=No; Interlocker Configuration=0 mm  [stored 0 ft]; Intruderprufe LowE SHGC Value=0.438; Intruderprufe LowE U Value=5.62; Intruderprufe SHGC Value=0.494; Intruderprufe U Value=6.84; Limit Sash Width Left Max=596 mm; Limit Sash Width Left Min=300 mm; Limit Window Width Max=2994 mm; Max Pane Area=0.28 m²; Outside Heavy Duty Interlocker=No; Sash Height=807 mm  [stored 2.64764 ft]; Sash Width Left=448 mm; Sash Width Right=448 mm; Standard Interlocker=Yes; Width=890 mm  [stored 2.91995 ft]; Windload Design=1500 mm  [stored 4.92126 ft]
- Elite-0909XX-2000Pa: Area Left Sash Glazing=0.28 m²; Area Right Sash Glazing=0.28 m²; Clearvue SHGC Value=0.521; Clearvue U Value=6.96; Custom Windload=2000 mm  [stored 6.56168 ft]; Custom Window Height=890 mm  [stored 2.91995 ft]; Custom Window Width=890 mm  [stored 2.91995 ft]; Energy Advantage SHGC Value=0.47; Energy Advantage U Value=5.88; Height=890 mm  [stored 2.91995 ft]; Inside Heavy Duty Interlocker=No; Interlocker Configuration=0 mm  [stored 0 ft]; Intruderprufe LowE SHGC Value=0.438; Intruderprufe LowE U Value=5.62; Intruderprufe SHGC Value=0.494; Intruderprufe U Value=6.84; Limit Sash Width Left Max=596 mm; Limit Sash Width Left Min=300 mm; Limit Window Width Max=2994 mm; Max Pane Area=0.28 m²; Outside Heavy Duty Interlocker=No; Sash Height=807 mm  [stored 2.64764 ft]; Sash Width Left=448 mm; Sash Width Right=448 mm; Standard Interlocker=Yes; Width=890 mm  [stored 2.91995 ft]; Windload Design=2000 mm  [stored 6.56168 ft]
- Elite-0912XX-1500Pa: Area Left Sash Glazing=0.39 m²; Area Right Sash Glazing=0.39 m²; Clearvue SHGC Value=0.553; Clearvue U Value=6.89; Custom Windload=1500 mm  [stored 4.92126 ft]; Custom Window Height=1190 mm  [stored 3.9042 ft]; Custom Window Width=890 mm  [stored 2.91995 ft]; Energy Advantage SHGC Value=0.4798; Energy Advantage U Value=5.72; Height=1190 mm  [stored 3.9042 ft]; Inside Heavy Duty Interlocker=No; Interlocker Configuration=0 mm  [stored 0 ft]; Intruderprufe LowE SHGC Value=0.464; Intruderprufe LowE U Value=5.35; Intruderprufe SHGC Value=0.525; Intruderprufe U Value=6.76; Limit Sash Width Left Max=596 mm; Limit Sash Width Left Min=300 mm; Limit Window Width Max=2994 mm; Max Pane Area=0.39 m²; Outside Heavy Duty Interlocker=No; Sash Height=1107 mm  [stored 3.63189 ft]; Sash Width Left=448 mm; Sash Width Right=448 mm; Standard Interlocker=Yes; Width=890 mm  [stored 2.91995 ft]; Windload Design=1500 mm  [stored 4.92126 ft]
- Elite-0912XX-2000Pa: Area Left Sash Glazing=0.39 m²; Area Right Sash Glazing=0.39 m²; Clearvue SHGC Value=0.553; Clearvue U Value=6.89; Custom Windload=2000 mm  [stored 6.56168 ft]; Custom Window Height=1190 mm  [stored 3.9042 ft]; Custom Window Width=890 mm  [stored 2.91995 ft]; Energy Advantage SHGC Value=0.4798; Energy Advantage U Value=5.72; Height=1190 mm  [stored 3.9042 ft]; Inside Heavy Duty Interlocker=No; Interlocker Configuration=0 mm  [stored 0 ft]; Intruderprufe LowE SHGC Value=0.464; Intruderprufe LowE U Value=5.35; Intruderprufe SHGC Value=0.525; Intruderprufe U Value=6.76; Limit Sash Width Left Max=596 mm; Limit Sash Width Left Min=300 mm; Limit Window Width Max=2994 mm; Max Pane Area=0.39 m²; Outside Heavy Duty Interlocker=No; Sash Height=1107 mm  [stored 3.63189 ft]; Sash Width Left=448 mm; Sash Width Right=448 mm; Standard Interlocker=Yes; Width=890 mm  [stored 2.91995 ft]; Windload Design=2000 mm  [stored 6.56168 ft]
- Elite-0915XX-1500Pa: Area Left Sash Glazing=0.51 m²; Area Right Sash Glazing=0.51 m²; Clearvue SHGC Value=0.572; Clearvue U Value=6.85; Custom Windload=1500 mm  [stored 4.92126 ft]; Custom Window Height=1490 mm  [stored 4.88845 ft]; Custom Window Width=890 mm  [stored 2.91995 ft]; Energy Advantage SHGC Value=0.515; Energy Advantage U Value=5.62; Height=1490 mm  [stored 4.88845 ft]; Inside Heavy Duty Interlocker=Yes; Interlocker Configuration=1 mm  [stored 0.00328084 ft]; Intruderprufe LowE SHGC Value=0.479; Intruderprufe LowE U Value=5.36; Intruderprufe SHGC Value=0.543; Intruderprufe U Value=6.72; Limit Sash Width Left Max=596 mm; Limit Sash Width Left Min=300 mm; Limit Window Width Max=2994 mm; Max Pane Area=0.51 m²; Outside Heavy Duty Interlocker=No; Sash Height=1407 mm  [stored 4.61614 ft]; Sash Width Left=448 mm; Sash Width Right=448 mm; Standard Interlocker=No; Width=890 mm  [stored 2.91995 ft]; Windload Design=1500 mm  [stored 4.92126 ft]
- Elite-0915XX-2000Pa: Area Left Sash Glazing=0.51 m²; Area Right Sash Glazing=0.51 m²; Clearvue SHGC Value=0.572; Clearvue U Value=6.85; Custom Windload=2000 mm  [stored 6.56168 ft]; Custom Window Height=1490 mm  [stored 4.88845 ft]; Custom Window Width=890 mm  [stored 2.91995 ft]; Energy Advantage SHGC Value=0.515; Energy Advantage U Value=5.62; Height=1490 mm  [stored 4.88845 ft]; Inside Heavy Duty Interlocker=Yes; Interlocker Configuration=1 mm  [stored 0.00328084 ft]; Intruderprufe LowE SHGC Value=0.479; Intruderprufe LowE U Value=5.36; Intruderprufe SHGC Value=0.543; Intruderprufe U Value=6.72; Limit Sash Width Left Max=596 mm; Limit Sash Width Left Min=300 mm; Limit Window Width Max=2994 mm; Max Pane Area=0.51 m²; Outside Heavy Duty Interlocker=No; Sash Height=1407 mm  [stored 4.61614 ft]; Sash Width Left=448 mm; Sash Width Right=448 mm; Standard Interlocker=No; Width=890 mm  [stored 2.91995 ft]; Windload Design=2000 mm  [stored 6.56168 ft]
- Elite-0918XX-1500Pa: Area Left Sash Glazing=0.62 m²; Area Right Sash Glazing=0.62 m²; Clearvue SHGC Value=0.585; Clearvue U Value=6.82; Custom Windload=1500 mm  [stored 4.92126 ft]; Custom Window Height=1790 mm  [stored 5.8727 ft]; Custom Window Width=890 mm  [stored 2.91995 ft]; Energy Advantage SHGC Value=0.526; Energy Advantage U Value=5.56; Height=1790 mm  [stored 5.8727 ft]; Inside Heavy Duty Interlocker=Yes; Interlocker Configuration=1 mm  [stored 0.00328084 ft]; Intruderprufe LowE SHGC Value=0.489; Intruderprufe LowE U Value=5.29; Intruderprufe SHGC Value=0.555; Intruderprufe U Value=6.69; Limit Sash Width Left Max=596 mm; Limit Sash Width Left Min=300 mm; Limit Window Width Max=1490 mm  [stored 4.88845 ft]; Max Pane Area=0.62 m²; Outside Heavy Duty Interlocker=No; Sash Height=1707 mm; Sash Width Left=448 mm; Sash Width Right=448 mm; Standard Interlocker=No; Width=890 mm  [stored 2.91995 ft]; Windload Design=1500 mm  [stored 4.92126 ft]
- Elite-0918XX-2000Pa: Area Left Sash Glazing=0.62 m²; Area Right Sash Glazing=0.62 m²; Clearvue SHGC Value=0.585; Clearvue U Value=6.82; Custom Windload=2000 mm  [stored 6.56168 ft]; Custom Window Height=1790 mm  [stored 5.8727 ft]; Custom Window Width=890 mm  [stored 2.91995 ft]; Energy Advantage SHGC Value=0.526; Energy Advantage U Value=5.56; Height=1790 mm  [stored 5.8727 ft]; Inside Heavy Duty Interlocker=Yes; Interlocker Configuration=2 mm  [stored 0.00656168 ft]; Intruderprufe LowE SHGC Value=0.489; Intruderprufe LowE U Value=5.29; Intruderprufe SHGC Value=0.555; Intruderprufe U Value=6.69; Limit Sash Width Left Max=596 mm; Limit Sash Width Left Min=300 mm; Limit Window Width Max=890 mm  [stored 2.91995 ft]; Max Pane Area=0.62 m²; Outside Heavy Duty Interlocker=Yes; Sash Height=1707 mm; Sash Width Left=448 mm; Sash Width Right=448 mm; Standard Interlocker=No; Width=890 mm  [stored 2.91995 ft]; Windload Design=2000 mm  [stored 6.56168 ft]
- Elite-1206XX-1500Pa: Area Left Sash Glazing=0.22 m²; Area Right Sash Glazing=0.22 m²; Clearvue SHGC Value=0.49; Clearvue U Value=7; Custom Windload=1500 mm  [stored 4.92126 ft]; Custom Window Height=590 mm  [stored 1.9357 ft]; Custom Window Width=1190 mm  [stored 3.9042 ft]; Energy Advantage SHGC Value=0.442; Energy Advantage U Value=5.95; Height=590 mm  [stored 1.9357 ft]; Inside Heavy Duty Interlocker=No; Interlocker Configuration=0 mm  [stored 0 ft]; Intruderprufe LowE SHGC Value=0.413; Intruderprufe LowE U Value=5.73; Intruderprufe SHGC Value=0.466; Intruderprufe U Value=6.88; Limit Sash Width Left Max=896 mm; Limit Sash Width Left Min=300 mm; Limit Window Width Max=2994 mm; Max Pane Area=0.22 m²; Outside Heavy Duty Interlocker=No; Sash Height=507 mm; Sash Width Left=598 mm; Sash Width Right=598 mm; Standard Interlocker=Yes; Width=1190 mm  [stored 3.9042 ft]; Windload Design=1500 mm  [stored 4.92126 ft]
- Elite-1206XX-2000Pa: Area Left Sash Glazing=0.22 m²; Area Right Sash Glazing=0.22 m²; Clearvue SHGC Value=0.49; Clearvue U Value=7; Custom Windload=2000 mm  [stored 6.56168 ft]; Custom Window Height=590 mm  [stored 1.9357 ft]; Custom Window Width=1190 mm  [stored 3.9042 ft]; Energy Advantage SHGC Value=0.442; Energy Advantage U Value=5.95; Height=590 mm  [stored 1.9357 ft]; Inside Heavy Duty Interlocker=No; Interlocker Configuration=0 mm  [stored 0 ft]; Intruderprufe LowE SHGC Value=0.413; Intruderprufe LowE U Value=5.73; Intruderprufe SHGC Value=0.466; Intruderprufe U Value=6.88; Limit Sash Width Left Max=896 mm; Limit Sash Width Left Min=300 mm; Limit Window Width Max=2994 mm; Max Pane Area=0.22 m²; Outside Heavy Duty Interlocker=No; Sash Height=507 mm; Sash Width Left=598 mm; Sash Width Right=598 mm; Standard Interlocker=Yes; Width=1190 mm  [stored 3.9042 ft]; Windload Design=2000 mm  [stored 6.56168 ft]
- Elite-1209XX-1500Pa: Area Left Sash Glazing=0.38 m²; Area Right Sash Glazing=0.38 m²; Clearvue SHGC Value=0.561; Clearvue U Value=6.82; Custom Windload=1500 mm  [stored 4.92126 ft]; Custom Window Height=890 mm  [stored 2.91995 ft]; Custom Window Width=1190 mm  [stored 3.9042 ft]; Energy Advantage SHGC Value=0.504; Energy Advantage U Value=5.58; Height=890 mm  [stored 2.91995 ft]; Inside Heavy Duty Interlocker=No; Interlocker Configuration=0 mm  [stored 0 ft]; Intruderprufe LowE SHGC Value=0.47; Intruderprufe LowE U Value=5.36; Intruderprufe SHGC Value=0.532; Intruderprufe U Value=6.7; Limit Sash Width Left Max=896 mm; Limit Sash Width Left Min=300 mm; Limit Window Width Max=2994 mm; Max Pane Area=0.38 m²; Outside Heavy Duty Interlocker=No; Sash Height=807 mm  [stored 2.64764 ft]; Sash Width Left=598 mm; Sash Width Right=598 mm; Standard Interlocker=Yes; Width=1190 mm  [stored 3.9042 ft]; Windload Design=1500 mm  [stored 4.92126 ft]
- Elite-1209XX-2000Pa: Area Left Sash Glazing=0.38 m²; Area Right Sash Glazing=0.38 m²; Clearvue SHGC Value=0.561; Clearvue U Value=6.82; Custom Windload=2000 mm  [stored 6.56168 ft]; Custom Window Height=890 mm  [stored 2.91995 ft]; Custom Window Width=1190 mm  [stored 3.9042 ft]; Energy Advantage SHGC Value=0.504; Energy Advantage U Value=5.58; Height=890 mm  [stored 2.91995 ft]; Inside Heavy Duty Interlocker=No; Interlocker Configuration=0 mm  [stored 0 ft]; Intruderprufe LowE SHGC Value=0.47; Intruderprufe LowE U Value=5.36; Intruderprufe SHGC Value=0.532; Intruderprufe U Value=6.7; Limit Sash Width Left Max=896 mm; Limit Sash Width Left Min=300 mm; Limit Window Width Max=2994 mm; Max Pane Area=0.38 m²; Outside Heavy Duty Interlocker=No; Sash Height=807 mm  [stored 2.64764 ft]; Sash Width Left=598 mm; Sash Width Right=598 mm; Standard Interlocker=Yes; Width=1190 mm  [stored 3.9042 ft]; Windload Design=2000 mm  [stored 6.56168 ft]
- Elite-1212XX-1500Pa: Area Left Sash Glazing=0.54 m²; Area Right Sash Glazing=0.54 m²; Clearvue SHGC Value=0.595; Clearvue U Value=6.73; Custom Windload=1500 mm  [stored 4.92126 ft]; Custom Window Height=1190 mm  [stored 3.9042 ft]; Custom Window Width=1190 mm  [stored 3.9042 ft]; Energy Advantage SHGC Value=0.535; Energy Advantage U Value=5.4; Height=1190 mm  [stored 3.9042 ft]; Inside Heavy Duty Interlocker=No; Interlocker Configuration=0 mm  [stored 0 ft]; Intruderprufe LowE SHGC Value=0.498; Intruderprufe LowE U Value=5.18; Intruderprufe SHGC Value=0.565; Intruderprufe U Value=6.61; Limit Sash Width Left Max=896 mm; Limit Sash Width Left Min=300 mm; Limit Window Width Max=2994 mm; Max Pane Area=0.54 m²; Outside Heavy Duty Interlocker=No; Sash Height=1107 mm  [stored 3.63189 ft]; Sash Width Left=598 mm; Sash Width Right=598 mm; Standard Interlocker=Yes; Width=1190 mm  [stored 3.9042 ft]; Windload Design=1500 mm  [stored 4.92126 ft]
- Elite-1212XX-2000Pa: Area Left Sash Glazing=0.54 m²; Area Right Sash Glazing=0.54 m²; Clearvue SHGC Value=0.595; Clearvue U Value=6.73; Custom Windload=2000 mm  [stored 6.56168 ft]; Custom Window Height=1190 mm  [stored 3.9042 ft]; Custom Window Width=1190 mm  [stored 3.9042 ft]; Energy Advantage SHGC Value=0.535; Energy Advantage U Value=5.4; Height=1190 mm  [stored 3.9042 ft]; Inside Heavy Duty Interlocker=Yes; Interlocker Configuration=1 mm  [stored 0.00328084 ft]; Intruderprufe LowE SHGC Value=0.498; Intruderprufe LowE U Value=5.18; Intruderprufe SHGC Value=0.565; Intruderprufe U Value=6.61; Limit Sash Width Left Max=896 mm; Limit Sash Width Left Min=300 mm; Limit Window Width Max=2994 mm; Max Pane Area=0.54 m²; Outside Heavy Duty Interlocker=No; Sash Height=1107 mm  [stored 3.63189 ft]; Sash Width Left=598 mm; Sash Width Right=598 mm; Standard Interlocker=No; Width=1190 mm  [stored 3.9042 ft]; Windload Design=2000 mm  [stored 6.56168 ft]
- Elite-1215XX-1500Pa: Area Left Sash Glazing=0.7 m²; Area Right Sash Glazing=0.7 m²; Clearvue SHGC Value=0.616; Clearvue U Value=6.68; Custom Windload=1500 mm  [stored 4.92126 ft]; Custom Window Height=1490 mm  [stored 4.88845 ft]; Custom Window Width=1190 mm  [stored 3.9042 ft]; Energy Advantage SHGC Value=0.554; Energy Advantage U Value=5.29; Height=1490 mm  [stored 4.88845 ft]; Inside Heavy Duty Interlocker=Yes; Interlocker Configuration=1 mm  [stored 0.00328084 ft]; Intruderprufe LowE SHGC Value=0.515; Intruderprufe LowE U Value=5.07; Intruderprufe SHGC Value=0.585; Intruderprufe U Value=6.55; Limit Sash Width Left Max=896 mm; Limit Sash Width Left Min=300 mm; Limit Window Width Max=2994 mm; Max Pane Area=0.7 m²; Outside Heavy Duty Interlocker=No; Sash Height=1407 mm  [stored 4.61614 ft]; Sash Width Left=598 mm; Sash Width Right=598 mm; Standard Interlocker=No; Width=1190 mm  [stored 3.9042 ft]; Windload Design=1500 mm  [stored 4.92126 ft]
- Elite-1215XX-2000Pa: Area Left Sash Glazing=0.7 m²; Area Right Sash Glazing=0.7 m²; Clearvue SHGC Value=0.616; Clearvue U Value=6.68; Custom Windload=2000 mm  [stored 6.56168 ft]; Custom Window Height=1490 mm  [stored 4.88845 ft]; Custom Window Width=1190 mm  [stored 3.9042 ft]; Energy Advantage SHGC Value=0.554; Energy Advantage U Value=5.29; Height=1490 mm  [stored 4.88845 ft]; Inside Heavy Duty Interlocker=Yes; Interlocker Configuration=1 mm  [stored 0.00328084 ft]; Intruderprufe LowE SHGC Value=0.515; Intruderprufe LowE U Value=5.07; Intruderprufe SHGC Value=0.585; Intruderprufe U Value=6.55; Limit Sash Width Left Max=896 mm; Limit Sash Width Left Min=300 mm; Limit Window Width Max=2994 mm; Max Pane Area=0.7 m²; Outside Heavy Duty Interlocker=No; Sash Height=1407 mm  [stored 4.61614 ft]; Sash Width Left=598 mm; Sash Width Right=598 mm; Standard Interlocker=No; Width=1190 mm  [stored 3.9042 ft]; Windload Design=2000 mm  [stored 6.56168 ft]
- Elite-1218XX-1500Pa: Area Left Sash Glazing=0.87 m²; Area Right Sash Glazing=0.87 m²; Clearvue SHGC Value=0.63; Clearvue U Value=6.64; Custom Windload=1500 mm  [stored 4.92126 ft]; Custom Window Height=1790 mm  [stored 5.8727 ft]; Custom Window Width=1190 mm  [stored 3.9042 ft]; Energy Advantage SHGC Value=0.566; Energy Advantage U Value=5.22; Height=1790 mm  [stored 5.8727 ft]; Inside Heavy Duty Interlocker=Yes; Interlocker Configuration=2 mm  [stored 0.00656168 ft]; Intruderprufe LowE SHGC Value=0.526; Intruderprufe LowE U Value=5; Intruderprufe SHGC Value=0.598; Intruderprufe U Value=6.52; Limit Sash Width Left Max=896 mm; Limit Sash Width Left Min=300 mm; Limit Window Width Max=1490 mm  [stored 4.88845 ft]; Max Pane Area=0.87 m²; Outside Heavy Duty Interlocker=Yes; Sash Height=1707 mm; Sash Width Left=598 mm; Sash Width Right=598 mm; Standard Interlocker=No; Width=1190 mm  [stored 3.9042 ft]; Windload Design=1500 mm  [stored 4.92126 ft]
- Elite-1506XX-1500Pa: Area Left Sash Glazing=0.28 m²; Area Right Sash Glazing=0.28 m²; Clearvue SHGC Value=0.511; Clearvue U Value=6.93; Custom Windload=1500 mm  [stored 4.92126 ft]; Custom Window Height=590 mm  [stored 1.9357 ft]; Custom Window Width=1490 mm  [stored 4.88845 ft]; Energy Advantage SHGC Value=0.46; Energy Advantage U Value=5.8; Height=590 mm  [stored 1.9357 ft]; Inside Heavy Duty Interlocker=No; Interlocker Configuration=0 mm  [stored 0 ft]; Intruderprufe LowE SHGC Value=0.429; Intruderprufe LowE U Value=5.61; Intruderprufe SHGC Value=0.485; Intruderprufe U Value=6.81; Limit Sash Width Left Max=1196 mm; Limit Sash Width Left Min=300 mm; Limit Window Width Max=2994 mm; Max Pane Area=0.28 m²; Outside Heavy Duty Interlocker=No; Sash Height=507 mm; Sash Width Left=748 mm; Sash Width Right=748 mm; Standard Interlocker=Yes; Width=1490 mm  [stored 4.88845 ft]; Windload Design=1500 mm  [stored 4.92126 ft]
- Elite-1506XX-2000Pa: Area Left Sash Glazing=0.28 m²; Area Right Sash Glazing=0.28 m²; Clearvue SHGC Value=0.511; Clearvue U Value=6.93; Custom Windload=2000 mm  [stored 6.56168 ft]; Custom Window Height=590 mm  [stored 1.9357 ft]; Custom Window Width=1490 mm  [stored 4.88845 ft]; Energy Advantage SHGC Value=0.46; Energy Advantage U Value=5.8; Height=590 mm  [stored 1.9357 ft]; Inside Heavy Duty Interlocker=No; Interlocker Configuration=0 mm  [stored 0 ft]; Intruderprufe LowE SHGC Value=0.429; Intruderprufe LowE U Value=5.61; Intruderprufe SHGC Value=0.485; Intruderprufe U Value=6.81; Limit Sash Width Left Max=1196 mm; Limit Sash Width Left Min=300 mm; Limit Window Width Max=2994 mm; Max Pane Area=0.28 m²; Outside Heavy Duty Interlocker=No; Sash Height=507 mm; Sash Width Left=748 mm; Sash Width Right=748 mm; Standard Interlocker=Yes; Width=1490 mm  [stored 4.88845 ft]; Windload Design=2000 mm  [stored 6.56168 ft]
- Elite-1509XX-1500Pa: Area Left Sash Glazing=0.49 m²; Area Right Sash Glazing=0.49 m²; Clearvue SHGC Value=0.584; Clearvue U Value=6.73; Custom Windload=1500 mm  [stored 4.92126 ft]; Custom Window Height=890 mm  [stored 2.91995 ft]; Custom Window Width=1490 mm  [stored 4.88845 ft]; Energy Advantage SHGC Value=0.525; Energy Advantage U Value=5.41; Height=890 mm  [stored 2.91995 ft]; Inside Heavy Duty Interlocker=No; Interlocker Configuration=0 mm  [stored 0 ft]; Intruderprufe LowE SHGC Value=0.489; Intruderprufe LowE U Value=5.21; Intruderprufe SHGC Value=0.55; Intruderprufe U Value=6.61; Limit Sash Width Left Max=1196 mm; Limit Sash Width Left Min=300 mm; Limit Window Width Max=2994 mm; Max Pane Area=0.49 m²; Outside Heavy Duty Interlocker=No; Sash Height=807 mm  [stored 2.64764 ft]; Sash Width Left=748 mm; Sash Width Right=748 mm; Standard Interlocker=Yes; Width=1490 mm  [stored 4.88845 ft]; Windload Design=1500 mm  [stored 4.92126 ft]
- Elite-1509XX-2000Pa: Area Left Sash Glazing=0.49 m²; Area Right Sash Glazing=0.49 m²; Clearvue SHGC Value=0.584; Clearvue U Value=6.73; Custom Windload=2000 mm  [stored 6.56168 ft]; Custom Window Height=890 mm  [stored 2.91995 ft]; Custom Window Width=1490 mm  [stored 4.88845 ft]; Energy Advantage SHGC Value=0.525; Energy Advantage U Value=5.41; Height=890 mm  [stored 2.91995 ft]; Inside Heavy Duty Interlocker=No; Interlocker Configuration=0 mm  [stored 0 ft]; Intruderprufe LowE SHGC Value=0.489; Intruderprufe LowE U Value=5.21; Intruderprufe SHGC Value=0.55; Intruderprufe U Value=6.61; Limit Sash Width Left Max=1196 mm; Limit Sash Width Left Min=300 mm; Limit Window Width Max=2994 mm; Max Pane Area=0.49 m²; Outside Heavy Duty Interlocker=No; Sash Height=807 mm  [stored 2.64764 ft]; Sash Width Left=748 mm; Sash Width Right=748 mm; Standard Interlocker=Yes; Width=1490 mm  [stored 4.88845 ft]; Windload Design=2000 mm  [stored 6.56168 ft]
- Elite-1512XX-1500Pa: Area Left Sash Glazing=0.7 m²; Area Right Sash Glazing=0.7 m²; Clearvue SHGC Value=0.621; Clearvue U Value=6.64; Custom Windload=1500 mm  [stored 4.92126 ft]; Custom Window Height=1190 mm  [stored 3.9042 ft]; Custom Window Width=1490 mm  [stored 4.88845 ft]; Energy Advantage SHGC Value=0.558; Energy Advantage U Value=5.21; Height=1190 mm  [stored 3.9042 ft]; Inside Heavy Duty Interlocker=Yes; Interlocker Configuration=1 mm  [stored 0.00328084 ft]; Intruderprufe LowE SHGC Value=0.519; Intruderprufe LowE U Value=5.01; Intruderprufe SHGC Value=0.589; Intruderprufe U Value=6.51; Limit Sash Width Left Max=1196 mm; Limit Sash Width Left Min=300 mm; Limit Window Width Max=2994 mm; Max Pane Area=0.7 m²; Outside Heavy Duty Interlocker=No; Sash Height=1107 mm  [stored 3.63189 ft]; Sash Width Left=748 mm; Sash Width Right=748 mm; Standard Interlocker=No; Width=1490 mm  [stored 4.88845 ft]; Windload Design=1500 mm  [stored 4.92126 ft]
- Elite-1512XX-2000Pa: Area Left Sash Glazing=0.7 m²; Area Right Sash Glazing=0.7 m²; Clearvue SHGC Value=0.621; Clearvue U Value=6.64; Custom Windload=2000 mm  [stored 6.56168 ft]; Custom Window Height=1190 mm  [stored 3.9042 ft]; Custom Window Width=1490 mm  [stored 4.88845 ft]; Energy Advantage SHGC Value=0.558; Energy Advantage U Value=5.21; Height=1190 mm  [stored 3.9042 ft]; Inside Heavy Duty Interlocker=Yes; Interlocker Configuration=1 mm  [stored 0.00328084 ft]; Intruderprufe LowE SHGC Value=0.519; Intruderprufe LowE U Value=5.01; Intruderprufe SHGC Value=0.589; Intruderprufe U Value=6.51; Limit Sash Width Left Max=1196 mm; Limit Sash Width Left Min=300 mm; Limit Window Width Max=2994 mm; Max Pane Area=0.7 m²; Outside Heavy Duty Interlocker=No; Sash Height=1107 mm  [stored 3.63189 ft]; Sash Width Left=748 mm; Sash Width Right=748 mm; Standard Interlocker=No; Width=1490 mm  [stored 4.88845 ft]; Windload Design=2000 mm  [stored 6.56168 ft]
- Elite-1515XX-1500Pa: Area Left Sash Glazing=0.9 m²; Area Right Sash Glazing=0.9 m²; Clearvue SHGC Value=0.643; Clearvue U Value=6.58; Custom Windload=1500 mm  [stored 4.92126 ft]; Custom Window Height=1490 mm  [stored 4.88845 ft]; Custom Window Width=1490 mm  [stored 4.88845 ft]; Energy Advantage SHGC Value=0.577; Energy Advantage U Value=5.09; Height=1490 mm  [stored 4.88845 ft]; Inside Heavy Duty Interlocker=Yes; Interlocker Configuration=1 mm  [stored 0.00328084 ft]; Intruderprufe LowE SHGC Value=0.537; Intruderprufe LowE U Value=4.9; Intruderprufe SHGC Value=0.61; Intruderprufe U Value=6.45; Limit Sash Width Left Max=1196 mm; Limit Sash Width Left Min=300 mm; Limit Window Width Max=2994 mm; Max Pane Area=0.9 m²; Outside Heavy Duty Interlocker=No; Sash Height=1407 mm  [stored 4.61614 ft]; Sash Width Left=748 mm; Sash Width Right=748 mm; Standard Interlocker=No; Width=1490 mm  [stored 4.88845 ft]; Windload Design=1500 mm  [stored 4.92126 ft]
- Elite-1515XX-2000Pa: Area Left Sash Glazing=0.9 m²; Area Right Sash Glazing=0.9 m²; Clearvue SHGC Value=0.643; Clearvue U Value=6.58; Custom Windload=2000 mm  [stored 6.56168 ft]; Custom Window Height=1490 mm  [stored 4.88845 ft]; Custom Window Width=1490 mm  [stored 4.88845 ft]; Energy Advantage SHGC Value=0.577; Energy Advantage U Value=5.09; Height=1490 mm  [stored 4.88845 ft]; Inside Heavy Duty Interlocker=Yes; Interlocker Configuration=2 mm  [stored 0.00656168 ft]; Intruderprufe LowE SHGC Value=0.537; Intruderprufe LowE U Value=4.9; Intruderprufe SHGC Value=0.61; Intruderprufe U Value=6.45; Limit Sash Width Left Max=1196 mm; Limit Sash Width Left Min=300 mm; Limit Window Width Max=2994 mm; Max Pane Area=0.9 m²; Outside Heavy Duty Interlocker=Yes; Sash Height=1407 mm  [stored 4.61614 ft]; Sash Width Left=748 mm; Sash Width Right=748 mm; Standard Interlocker=No; Width=1490 mm  [stored 4.88845 ft]; Windload Design=2000 mm  [stored 6.56168 ft]
- Elite-1518XX-1500Pa: Area Left Sash Glazing=1.11 m²; Area Right Sash Glazing=1.11 m²; Clearvue SHGC Value=0.657; Clearvue U Value=6.54; Custom Windload=1500 mm  [stored 4.92126 ft]; Custom Window Height=1790 mm  [stored 5.8727 ft]; Custom Window Width=1490 mm  [stored 4.88845 ft]; Energy Advantage SHGC Value=0.59; Energy Advantage U Value=5.01; Height=1790 mm  [stored 5.8727 ft]; Inside Heavy Duty Interlocker=Yes; Interlocker Configuration=2 mm  [stored 0.00656168 ft]; Intruderprufe LowE SHGC Value=0.548; Intruderprufe LowE U Value=4.82; Intruderprufe SHGC Value=0.624; Intruderprufe U Value=6.41; Limit Sash Width Left Max=1196 mm; Limit Sash Width Left Min=300 mm; Limit Window Width Max=1490 mm  [stored 4.88845 ft]; Max Pane Area=1.11 m²; Outside Heavy Duty Interlocker=Yes; Sash Height=1707 mm; Sash Width Left=748 mm; Sash Width Right=748 mm; Standard Interlocker=No; Width=1490 mm  [stored 4.88845 ft]; Windload Design=1500 mm  [stored 4.92126 ft]
- Elite-1806XX-1500Pa: Area Left Sash Glazing=0.35 m²; Area Right Sash Glazing=0.35 m²; Clearvue SHGC Value=0.524; Clearvue U Value=6.88; Custom Windload=1500 mm  [stored 4.92126 ft]; Custom Window Height=590 mm  [stored 1.9357 ft]; Custom Window Width=1790 mm  [stored 5.8727 ft]; Energy Advantage SHGC Value=0.472; Energy Advantage U Value=5.7; Height=590 mm  [stored 1.9357 ft]; Inside Heavy Duty Interlocker=No; Interlocker Configuration=0 mm  [stored 0 ft]; Intruderprufe LowE SHGC Value=0.44; Intruderprufe LowE U Value=5.52; Intruderprufe SHGC Value=0.498; Intruderprufe U Value=6.76; Limit Sash Width Left Max=1496 mm; Limit Sash Width Left Min=300 mm; Limit Window Width Max=2994 mm; Max Pane Area=0.35 m²; Outside Heavy Duty Interlocker=No; Sash Height=507 mm; Sash Width Left=898 mm; Sash Width Right=898 mm; Standard Interlocker=Yes; Width=1790 mm  [stored 5.8727 ft]; Windload Design=1500 mm  [stored 4.92126 ft]
- Elite-1806XX-2000Pa: Area Left Sash Glazing=0.35 m²; Area Right Sash Glazing=0.35 m²; Clearvue SHGC Value=0.524; Clearvue U Value=6.88; Custom Windload=2000 mm  [stored 6.56168 ft]; Custom Window Height=590 mm  [stored 1.9357 ft]; Custom Window Width=1790 mm  [stored 5.8727 ft]; Energy Advantage SHGC Value=0.472; Energy Advantage U Value=5.7; Height=590 mm  [stored 1.9357 ft]; Inside Heavy Duty Interlocker=No; Interlocker Configuration=0 mm  [stored 0 ft]; Intruderprufe LowE SHGC Value=0.44; Intruderprufe LowE U Value=5.52; Intruderprufe SHGC Value=0.498; Intruderprufe U Value=6.76; Limit Sash Width Left Max=1496 mm; Limit Sash Width Left Min=300 mm; Limit Window Width Max=2994 mm; Max Pane Area=0.35 m²; Outside Heavy Duty Interlocker=No; Sash Height=507 mm; Sash Width Left=898 mm; Sash Width Right=898 mm; Standard Interlocker=Yes; Width=1790 mm  [stored 5.8727 ft]; Windload Design=2000 mm  [stored 6.56168 ft]
- Elite-1809XX-1500Pa: Area Left Sash Glazing=0.6 m²; Area Right Sash Glazing=0.6 m²; Clearvue SHGC Value=2.6; Clearvue U Value=6.68; Custom Windload=1500 mm  [stored 4.92126 ft]; Custom Window Height=890 mm  [stored 2.91995 ft]; Custom Window Width=1790 mm  [stored 5.8727 ft]; Energy Advantage SHGC Value=0.539; Energy Advantage U Value=5.29; Height=890 mm  [stored 2.91995 ft]; Inside Heavy Duty Interlocker=No; Interlocker Configuration=0 mm  [stored 0 ft]; Intruderprufe LowE SHGC Value=0.502; Intruderprufe LowE U Value=5.11; Intruderprufe SHGC Value=0.57; Intruderprufe U Value=6.55; Limit Sash Width Left Max=1496 mm; Limit Sash Width Left Min=300 mm; Limit Window Width Max=2994 mm; Max Pane Area=0.6 m²; Outside Heavy Duty Interlocker=No; Sash Height=807 mm  [stored 2.64764 ft]; Sash Width Left=898 mm; Sash Width Right=898 mm; Standard Interlocker=Yes; Width=1790 mm  [stored 5.8727 ft]; Windload Design=1500 mm  [stored 4.92126 ft]
- Elite-1809XX-2000Pa: Area Left Sash Glazing=0.6 m²; Area Right Sash Glazing=0.6 m²; Clearvue SHGC Value=2.6; Clearvue U Value=6.68; Custom Windload=2000 mm  [stored 6.56168 ft]; Custom Window Height=890 mm  [stored 2.91995 ft]; Custom Window Width=1790 mm  [stored 5.8727 ft]; Energy Advantage SHGC Value=0.539; Energy Advantage U Value=5.29; Height=890 mm  [stored 2.91995 ft]; Inside Heavy Duty Interlocker=No; Interlocker Configuration=0 mm  [stored 0 ft]; Intruderprufe LowE SHGC Value=0.502; Intruderprufe LowE U Value=5.11; Intruderprufe SHGC Value=0.57; Intruderprufe U Value=6.55; Limit Sash Width Left Max=1496 mm; Limit Sash Width Left Min=300 mm; Limit Window Width Max=2994 mm; Max Pane Area=0.6 m²; Outside Heavy Duty Interlocker=No; Sash Height=807 mm  [stored 2.64764 ft]; Sash Width Left=898 mm; Sash Width Right=898 mm; Standard Interlocker=Yes; Width=1790 mm  [stored 5.8727 ft]; Windload Design=2000 mm  [stored 6.56168 ft]
- Elite-1812XX-1500Pa: Area Left Sash Glazing=0.85 m²; Area Right Sash Glazing=0.85 m²; Clearvue SHGC Value=0.638; Clearvue U Value=6.57; Custom Windload=1500 mm  [stored 4.92126 ft]; Custom Window Height=1190 mm  [stored 3.9042 ft]; Custom Window Width=1790 mm  [stored 5.8727 ft]; Energy Advantage SHGC Value=0.572; Energy Advantage U Value=5.08; Height=1190 mm  [stored 3.9042 ft]; Inside Heavy Duty Interlocker=Yes; Interlocker Configuration=1 mm  [stored 0.00328084 ft]; Intruderprufe LowE SHGC Value=0.533; Intruderprufe LowE U Value=4.91; Intruderprufe SHGC Value=0.605; Intruderprufe U Value=6.45; Limit Sash Width Left Max=1496 mm; Limit Sash Width Left Min=300 mm; Limit Window Width Max=2994 mm; Max Pane Area=0.85 m²; Outside Heavy Duty Interlocker=No; Sash Height=1107 mm  [stored 3.63189 ft]; Sash Width Left=898 mm; Sash Width Right=898 mm; Standard Interlocker=No; Width=1790 mm  [stored 5.8727 ft]; Windload Design=1500 mm  [stored 4.92126 ft]
- Elite-1812XX-2000Pa: Area Left Sash Glazing=0.85 m²; Area Right Sash Glazing=0.85 m²; Clearvue SHGC Value=0.638; Clearvue U Value=6.57; Custom Windload=2000 mm  [stored 6.56168 ft]; Custom Window Height=1190 mm  [stored 3.9042 ft]; Custom Window Width=1790 mm  [stored 5.8727 ft]; Energy Advantage SHGC Value=0.572; Energy Advantage U Value=5.08; Height=1190 mm  [stored 3.9042 ft]; Inside Heavy Duty Interlocker=Yes; Interlocker Configuration=1 mm  [stored 0.00328084 ft]; Intruderprufe LowE SHGC Value=0.533; Intruderprufe LowE U Value=4.91; Intruderprufe SHGC Value=0.605; Intruderprufe U Value=6.45; Limit Sash Width Left Max=1496 mm; Limit Sash Width Left Min=300 mm; Limit Window Width Max=2994 mm; Max Pane Area=0.85 m²; Outside Heavy Duty Interlocker=No; Sash Height=1107 mm  [stored 3.63189 ft]; Sash Width Left=898 mm; Sash Width Right=898 mm; Standard Interlocker=No; Width=1790 mm  [stored 5.8727 ft]; Windload Design=2000 mm  [stored 6.56168 ft]
- Elite-1815XX-1500Pa: Area Left Sash Glazing=1.1 m²; Area Right Sash Glazing=1.1 m²; Clearvue SHGC Value=0.66; Clearvue U Value=6.51; Custom Windload=1500 mm  [stored 4.92126 ft]; Custom Window Height=1490 mm  [stored 4.88845 ft]; Custom Window Width=1790 mm  [stored 5.8727 ft]; Energy Advantage SHGC Value=0.592; Energy Advantage U Value=4.96; Height=1490 mm  [stored 4.88845 ft]; Inside Heavy Duty Interlocker=Yes; Interlocker Configuration=1 mm  [stored 0.00328084 ft]; Intruderprufe LowE SHGC Value=0.551; Intruderprufe LowE U Value=4.78; Intruderprufe SHGC Value=0.627; Intruderprufe U Value=6.39; Limit Sash Width Left Max=1496 mm; Limit Sash Width Left Min=300 mm; Limit Window Width Max=2994 mm; Max Pane Area=1.1 m²; Outside Heavy Duty Interlocker=No; Sash Height=1407 mm  [stored 4.61614 ft]; Sash Width Left=898 mm; Sash Width Right=898 mm; Standard Interlocker=No; Width=1790 mm  [stored 5.8727 ft]; Windload Design=1500 mm  [stored 4.92126 ft]
- Elite-1815XX-2000Pa: Area Left Sash Glazing=1.1 m²; Area Right Sash Glazing=1.1 m²; Clearvue SHGC Value=0.66; Clearvue U Value=6.51; Custom Windload=2000 mm  [stored 6.56168 ft]; Custom Window Height=1490 mm  [stored 4.88845 ft]; Custom Window Width=1790 mm  [stored 5.8727 ft]; Energy Advantage SHGC Value=0.592; Energy Advantage U Value=4.96; Height=1490 mm  [stored 4.88845 ft]; Inside Heavy Duty Interlocker=Yes; Interlocker Configuration=2 mm  [stored 0.00656168 ft]; Intruderprufe LowE SHGC Value=0.551; Intruderprufe LowE U Value=4.78; Intruderprufe SHGC Value=0.627; Intruderprufe U Value=6.39; Limit Sash Width Left Max=1496 mm; Limit Sash Width Left Min=300 mm; Limit Window Width Max=2994 mm; Max Pane Area=1.1 m²; Outside Heavy Duty Interlocker=Yes; Sash Height=1407 mm  [stored 4.61614 ft]; Sash Width Left=898 mm; Sash Width Right=898 mm; Standard Interlocker=No; Width=1790 mm  [stored 5.8727 ft]; Windload Design=2000 mm  [stored 6.56168 ft]
- Elite-2106XX-1500Pa: Area Left Sash Glazing=0.41 m²; Area Right Sash Glazing=0.41 m²; Clearvue SHGC Value=0.534; Clearvue U Value=6.85; Custom Windload=1500 mm  [stored 4.92126 ft]; Custom Window Height=590 mm  [stored 1.9357 ft]; Custom Window Width=2090 mm  [stored 6.85696 ft]; Energy Advantage SHGC Value=0.48; Energy Advantage U Value=5.63; Height=590 mm  [stored 1.9357 ft]; Inside Heavy Duty Interlocker=No; Interlocker Configuration=0 mm  [stored 0 ft]; Intruderprufe LowE SHGC Value=0.448; Intruderprufe LowE U Value=5.46; Intruderprufe SHGC Value=0.507; Intruderprufe U Value=6.763; Limit Sash Width Left Max=1500 mm  [stored 4.92126 ft]; Limit Sash Width Left Min=596 mm; Limit Window Width Max=2994 mm; Max Pane Area=0.41 m²; Outside Heavy Duty Interlocker=No; Sash Height=507 mm; Sash Width Left=1048 mm; Sash Width Right=1048 mm; Standard Interlocker=Yes; Width=2090 mm  [stored 6.85696 ft]; Windload Design=1500 mm  [stored 4.92126 ft]
- Elite-2106XX-2000Pa: Area Left Sash Glazing=0.41 m²; Area Right Sash Glazing=0.41 m²; Clearvue SHGC Value=0.534; Clearvue U Value=6.85; Custom Windload=2000 mm  [stored 6.56168 ft]; Custom Window Height=590 mm  [stored 1.9357 ft]; Custom Window Width=2090 mm  [stored 6.85696 ft]; Energy Advantage SHGC Value=0.48; Energy Advantage U Value=5.63; Height=590 mm  [stored 1.9357 ft]; Inside Heavy Duty Interlocker=No; Interlocker Configuration=0 mm  [stored 0 ft]; Intruderprufe LowE SHGC Value=0.448; Intruderprufe LowE U Value=5.46; Intruderprufe SHGC Value=0.507; Intruderprufe U Value=6.763; Limit Sash Width Left Max=1500 mm  [stored 4.92126 ft]; Limit Sash Width Left Min=596 mm; Limit Window Width Max=2994 mm; Max Pane Area=0.41 m²; Outside Heavy Duty Interlocker=No; Sash Height=507 mm; Sash Width Left=1048 mm; Sash Width Right=1048 mm; Standard Interlocker=Yes; Width=2090 mm  [stored 6.85696 ft]; Windload Design=2000 mm  [stored 6.56168 ft]
- Elite-2109XX-1500Pa: Area Left Sash Glazing=0.7 m²; Area Right Sash Glazing=0.7 m²; Clearvue SHGC Value=0.611; Clearvue U Value=6.64; Custom Windload=1500 mm  [stored 4.92126 ft]; Custom Window Height=890 mm  [stored 2.91995 ft]; Custom Window Width=2090 mm  [stored 6.85696 ft]; Energy Advantage SHGC Value=0.549; Energy Advantage U Value=5.2; Height=890 mm  [stored 2.91995 ft]; Inside Heavy Duty Interlocker=No; Interlocker Configuration=0 mm  [stored 0 ft]; Intruderprufe LowE SHGC Value=0.511; Intruderprufe LowE U Value=5.04; Intruderprufe SHGC Value=0.58; Intruderprufe U Value=6.54; Limit Sash Width Left Max=1500 mm  [stored 4.92126 ft]; Limit Sash Width Left Min=596 mm; Limit Window Width Max=2994 mm; Max Pane Area=0.7 m²; Outside Heavy Duty Interlocker=No; Sash Height=807 mm  [stored 2.64764 ft]; Sash Width Left=1048 mm; Sash Width Right=1048 mm; Standard Interlocker=Yes; Width=2090 mm  [stored 6.85696 ft]; Windload Design=1500 mm  [stored 4.92126 ft]
- Elite-2109XX-2000Pa: Area Left Sash Glazing=0.7 m²; Area Right Sash Glazing=0.7 m²; Clearvue SHGC Value=0.611; Clearvue U Value=6.64; Custom Windload=2000 mm  [stored 6.56168 ft]; Custom Window Height=890 mm  [stored 2.91995 ft]; Custom Window Width=2090 mm  [stored 6.85696 ft]; Energy Advantage SHGC Value=0.549; Energy Advantage U Value=5.2; Height=890 mm  [stored 2.91995 ft]; Inside Heavy Duty Interlocker=No; Interlocker Configuration=0 mm  [stored 0 ft]; Intruderprufe LowE SHGC Value=0.511; Intruderprufe LowE U Value=5.04; Intruderprufe SHGC Value=0.58; Intruderprufe U Value=6.54; Limit Sash Width Left Max=1500 mm  [stored 4.92126 ft]; Limit Sash Width Left Min=596 mm; Limit Window Width Max=2994 mm; Max Pane Area=0.7 m²; Outside Heavy Duty Interlocker=No; Sash Height=807 mm  [stored 2.64764 ft]; Sash Width Left=1048 mm; Sash Width Right=1048 mm; Standard Interlocker=Yes; Width=2090 mm  [stored 6.85696 ft]; Windload Design=2000 mm  [stored 6.56168 ft]
- Elite-2112XX-1500Pa: Area Left Sash Glazing=1 m²; Area Right Sash Glazing=1 m²; Clearvue SHGC Value=0.65; Clearvue U Value=6.53; Custom Windload=1500 mm  [stored 4.92126 ft]; Custom Window Height=1190 mm  [stored 3.9042 ft]; Custom Window Width=2090 mm  [stored 6.85696 ft]; Energy Advantage SHGC Value=0.583; Energy Advantage U Value=4.99; Height=1190 mm  [stored 3.9042 ft]; Inside Heavy Duty Interlocker=Yes; Interlocker Configuration=1 mm  [stored 0.00328084 ft]; Intruderprufe LowE SHGC Value=0.542; Intruderprufe LowE U Value=4.83; Intruderprufe SHGC Value=0.617; Intruderprufe U Value=6.4; Limit Sash Width Left Max=1500 mm  [stored 4.92126 ft]; Limit Sash Width Left Min=596 mm; Limit Window Width Max=2994 mm; Max Pane Area=1 m²; Outside Heavy Duty Interlocker=No; Sash Height=1107 mm  [stored 3.63189 ft]; Sash Width Left=1048 mm; Sash Width Right=1048 mm; Standard Interlocker=No; Width=2090 mm  [stored 6.85696 ft]; Windload Design=1500 mm  [stored 4.92126 ft]
- Elite-2112XX-2000Pa: Area Left Sash Glazing=1 m²; Area Right Sash Glazing=1 m²; Clearvue SHGC Value=0.65; Clearvue U Value=6.53; Custom Windload=2000 mm  [stored 6.56168 ft]; Custom Window Height=1190 mm  [stored 3.9042 ft]; Custom Window Width=2090 mm  [stored 6.85696 ft]; Energy Advantage SHGC Value=0.583; Energy Advantage U Value=4.99; Height=1190 mm  [stored 3.9042 ft]; Inside Heavy Duty Interlocker=Yes; Interlocker Configuration=1 mm  [stored 0.00328084 ft]; Intruderprufe LowE SHGC Value=0.542; Intruderprufe LowE U Value=4.83; Intruderprufe SHGC Value=0.617; Intruderprufe U Value=6.4; Limit Sash Width Left Max=1500 mm  [stored 4.92126 ft]; Limit Sash Width Left Min=596 mm; Limit Window Width Max=2994 mm; Max Pane Area=1 m²; Outside Heavy Duty Interlocker=No; Sash Height=1107 mm  [stored 3.63189 ft]; Sash Width Left=1048 mm; Sash Width Right=1048 mm; Standard Interlocker=No; Width=2090 mm  [stored 6.85696 ft]; Windload Design=2000 mm  [stored 6.56168 ft]
- Elite-2115XX-1500Pa: Area Left Sash Glazing=1.3 m²; Area Right Sash Glazing=1.3 m²; Clearvue SHGC Value=0.673; Clearvue U Value=6.47; Custom Windload=1500 mm  [stored 4.92126 ft]; Custom Window Height=1490 mm  [stored 4.88845 ft]; Custom Window Width=2090 mm  [stored 6.85696 ft]; Energy Advantage SHGC Value=0.603; Energy Advantage U Value=4.86; Height=1490 mm  [stored 4.88845 ft]; Inside Heavy Duty Interlocker=Yes; Interlocker Configuration=2 mm  [stored 0.00656168 ft]; Intruderprufe LowE SHGC Value=0.561; Intruderprufe LowE U Value=4.7; Intruderprufe SHGC Value=0.638; Intruderprufe U Value=6.34; Limit Sash Width Left Max=1500 mm  [stored 4.92126 ft]; Limit Sash Width Left Min=596 mm; Limit Window Width Max=2994 mm; Max Pane Area=1.3 m²; Outside Heavy Duty Interlocker=Yes; Sash Height=1407 mm  [stored 4.61614 ft]; Sash Width Left=1048 mm; Sash Width Right=1048 mm; Standard Interlocker=No; Width=2090 mm  [stored 6.85696 ft]; Windload Design=1500 mm  [stored 4.92126 ft]
- Elite-2115XX-2000Pa: Area Left Sash Glazing=1.3 m²; Area Right Sash Glazing=1.3 m²; Clearvue SHGC Value=0.673; Clearvue U Value=6.47; Custom Windload=2000 mm  [stored 6.56168 ft]; Custom Window Height=1490 mm  [stored 4.88845 ft]; Custom Window Width=2090 mm  [stored 6.85696 ft]; Energy Advantage SHGC Value=0.603; Energy Advantage U Value=4.86; Height=1490 mm  [stored 4.88845 ft]; Inside Heavy Duty Interlocker=Yes; Interlocker Configuration=2 mm  [stored 0.00656168 ft]; Intruderprufe LowE SHGC Value=0.561; Intruderprufe LowE U Value=4.7; Intruderprufe SHGC Value=0.638; Intruderprufe U Value=6.34; Limit Sash Width Left Max=1500 mm  [stored 4.92126 ft]; Limit Sash Width Left Min=596 mm; Limit Window Width Max=2994 mm; Max Pane Area=1.3 m²; Outside Heavy Duty Interlocker=Yes; Sash Height=1407 mm  [stored 4.61614 ft]; Sash Width Left=1048 mm; Sash Width Right=1048 mm; Standard Interlocker=No; Width=2090 mm  [stored 6.85696 ft]; Windload Design=2000 mm  [stored 6.56168 ft]
- Elite-2406XX-1500Pa: Area Left Sash Glazing=0.47 m²; Area Right Sash Glazing=0.47 m²; Clearvue SHGC Value=0.541; Clearvue U Value=6.82; Custom Windload=1500 mm  [stored 4.92126 ft]; Custom Window Height=590 mm  [stored 1.9357 ft]; Custom Window Width=2390 mm  [stored 7.84121 ft]; Energy Advantage SHGC Value=0.487; Energy Advantage U Value=5.58; Height=590 mm  [stored 1.9357 ft]; Inside Heavy Duty Interlocker=No; Interlocker Configuration=0 mm  [stored 0 ft]; Intruderprufe LowE SHGC Value=0.454; Intruderprufe LowE U Value=5.42; Intruderprufe SHGC Value=0.514; Intruderprufe U Value=6.7; Limit Sash Width Left Max=1500 mm  [stored 4.92126 ft]; Limit Sash Width Left Min=896 mm; Limit Window Width Max=2994 mm; Max Pane Area=0.47 m²; Outside Heavy Duty Interlocker=No; Sash Height=507 mm; Sash Width Left=1198 mm; Sash Width Right=1198 mm; Standard Interlocker=Yes; Width=2390 mm  [stored 7.84121 ft]; Windload Design=1500 mm  [stored 4.92126 ft]
- Elite-2406XX-2000Pa: Area Left Sash Glazing=0.47 m²; Area Right Sash Glazing=0.47 m²; Clearvue SHGC Value=0.541; Clearvue U Value=6.82; Custom Windload=2000 mm  [stored 6.56168 ft]; Custom Window Height=590 mm  [stored 1.9357 ft]; Custom Window Width=2390 mm  [stored 7.84121 ft]; Energy Advantage SHGC Value=0.487; Energy Advantage U Value=5.58; Height=590 mm  [stored 1.9357 ft]; Inside Heavy Duty Interlocker=No; Interlocker Configuration=0 mm  [stored 0 ft]; Intruderprufe LowE SHGC Value=0.454; Intruderprufe LowE U Value=5.42; Intruderprufe SHGC Value=0.514; Intruderprufe U Value=6.7; Limit Sash Width Left Max=1500 mm  [stored 4.92126 ft]; Limit Sash Width Left Min=896 mm; Limit Window Width Max=2994 mm; Max Pane Area=0.47 m²; Outside Heavy Duty Interlocker=No; Sash Height=507 mm; Sash Width Left=1198 mm; Sash Width Right=1198 mm; Standard Interlocker=Yes; Width=2390 mm  [stored 7.84121 ft]; Windload Design=2000 mm  [stored 6.56168 ft]
- Elite-2409XX-1500Pa: Area Left Sash Glazing=0.81 m²; Area Right Sash Glazing=0.81 m²; Clearvue SHGC Value=0.62; Clearvue U Value=6.6; Custom Windload=1500 mm  [stored 4.92126 ft]; Custom Window Height=890 mm  [stored 2.91995 ft]; Custom Window Width=2390 mm  [stored 7.84121 ft]; Energy Advantage SHGC Value=0.556; Energy Advantage U Value=5.14; Height=890 mm  [stored 2.91995 ft]; Inside Heavy Duty Interlocker=No; Interlocker Configuration=0 mm  [stored 0 ft]; Intruderprufe LowE SHGC Value=0.518; Intruderprufe LowE U Value=4.99; Intruderprufe SHGC Value=0.588; Intruderprufe U Value=6.48; Limit Sash Width Left Max=1500 mm  [stored 4.92126 ft]; Limit Sash Width Left Min=896 mm; Limit Window Width Max=2994 mm; Max Pane Area=0.81 m²; Outside Heavy Duty Interlocker=No; Sash Height=807 mm  [stored 2.64764 ft]; Sash Width Left=1198 mm; Sash Width Right=1198 mm; Standard Interlocker=Yes; Width=2390 mm  [stored 7.84121 ft]; Windload Design=1500 mm  [stored 4.92126 ft]
- Elite-2409XX-2000Pa: Area Left Sash Glazing=0.81 m²; Area Right Sash Glazing=0.81 m²; Clearvue SHGC Value=0.62; Clearvue U Value=6.6; Custom Windload=2000 mm  [stored 6.56168 ft]; Custom Window Height=890 mm  [stored 2.91995 ft]; Custom Window Width=2390 mm  [stored 7.84121 ft]; Energy Advantage SHGC Value=0.556; Energy Advantage U Value=5.14; Height=890 mm  [stored 2.91995 ft]; Inside Heavy Duty Interlocker=No; Interlocker Configuration=0 mm  [stored 0 ft]; Intruderprufe LowE SHGC Value=0.518; Intruderprufe LowE U Value=4.99; Intruderprufe SHGC Value=0.588; Intruderprufe U Value=6.48; Limit Sash Width Left Max=1500 mm  [stored 4.92126 ft]; Limit Sash Width Left Min=896 mm; Limit Window Width Max=2994 mm; Max Pane Area=0.81 m²; Outside Heavy Duty Interlocker=No; Sash Height=807 mm  [stored 2.64764 ft]; Sash Width Left=1198 mm; Sash Width Right=1198 mm; Standard Interlocker=Yes; Width=2390 mm  [stored 7.84121 ft]; Windload Design=2000 mm  [stored 6.56168 ft]
- Elite-2412XX-1500Pa: Area Left Sash Glazing=1.15 m²; Area Right Sash Glazing=1.15 m²; Clearvue SHGC Value=0.659; Clearvue U Value=6.5; Custom Windload=1500 mm  [stored 4.92126 ft]; Custom Window Height=1190 mm  [stored 3.9042 ft]; Custom Window Width=2390 mm  [stored 7.84121 ft]; Energy Advantage SHGC Value=0.591; Energy Advantage U Value=4.92; Height=1190 mm  [stored 3.9042 ft]; Inside Heavy Duty Interlocker=Yes; Interlocker Configuration=1 mm  [stored 0.00328084 ft]; Intruderprufe LowE SHGC Value=0.55; Intruderprufe LowE U Value=4.77; Intruderprufe SHGC Value=0.625; Intruderprufe U Value=6.37; Limit Sash Width Left Max=1500 mm  [stored 4.92126 ft]; Limit Sash Width Left Min=896 mm; Limit Window Width Max=2994 mm; Max Pane Area=1.15 m²; Outside Heavy Duty Interlocker=No; Sash Height=1107 mm  [stored 3.63189 ft]; Sash Width Left=1198 mm; Sash Width Right=1198 mm; Standard Interlocker=No; Width=2390 mm  [stored 7.84121 ft]; Windload Design=1500 mm  [stored 4.92126 ft]
- Elite-2412XX-2000Pa: Area Left Sash Glazing=1.15 m²; Area Right Sash Glazing=1.15 m²; Clearvue SHGC Value=0.659; Clearvue U Value=6.5; Custom Windload=2000 mm  [stored 6.56168 ft]; Custom Window Height=1190 mm  [stored 3.9042 ft]; Custom Window Width=2390 mm  [stored 7.84121 ft]; Energy Advantage SHGC Value=0.591; Energy Advantage U Value=4.92; Height=1190 mm  [stored 3.9042 ft]; Inside Heavy Duty Interlocker=Yes; Interlocker Configuration=1 mm  [stored 0.00328084 ft]; Intruderprufe LowE SHGC Value=0.55; Intruderprufe LowE U Value=4.77; Intruderprufe SHGC Value=0.625; Intruderprufe U Value=6.37; Limit Sash Width Left Max=1500 mm  [stored 4.92126 ft]; Limit Sash Width Left Min=896 mm; Limit Window Width Max=2994 mm; Max Pane Area=1.15 m²; Outside Heavy Duty Interlocker=No; Sash Height=1107 mm  [stored 3.63189 ft]; Sash Width Left=1198 mm; Sash Width Right=1198 mm; Standard Interlocker=No; Width=2390 mm  [stored 7.84121 ft]; Windload Design=2000 mm  [stored 6.56168 ft]
- Elite-2415XX-1500Pa: Area Left Sash Glazing=1.49 m²; Area Right Sash Glazing=1.49 m²; Clearvue SHGC Value=0.682; Clearvue U Value=6.43; Custom Windload=1500 mm  [stored 4.92126 ft]; Custom Window Height=1490 mm  [stored 4.88845 ft]; Custom Window Width=2390 mm  [stored 7.84121 ft]; Energy Advantage SHGC Value=0.611; Energy Advantage U Value=4.79; Height=1490 mm  [stored 4.88845 ft]; Inside Heavy Duty Interlocker=Yes; Interlocker Configuration=2 mm  [stored 0.00656168 ft]; Intruderprufe LowE SHGC Value=0.569; Intruderprufe LowE U Value=4.64; Intruderprufe SHGC Value=0.647; Intruderprufe U Value=6.31; Limit Sash Width Left Max=1500 mm  [stored 4.92126 ft]; Limit Sash Width Left Min=896 mm; Limit Window Width Max=2994 mm; Max Pane Area=1.49 m²; Outside Heavy Duty Interlocker=Yes; Sash Height=1407 mm  [stored 4.61614 ft]; Sash Width Left=1198 mm; Sash Width Right=1198 mm; Standard Interlocker=No; Width=2390 mm  [stored 7.84121 ft]; Windload Design=1500 mm  [stored 4.92126 ft]
- Elite-2415XX-2000Pa: Area Left Sash Glazing=1.49 m²; Area Right Sash Glazing=1.49 m²; Clearvue SHGC Value=0.682; Clearvue U Value=6.43; Custom Windload=2000 mm  [stored 6.56168 ft]; Custom Window Height=1490 mm  [stored 4.88845 ft]; Custom Window Width=2390 mm  [stored 7.84121 ft]; Energy Advantage SHGC Value=0.611; Energy Advantage U Value=4.79; Height=1490 mm  [stored 4.88845 ft]; Inside Heavy Duty Interlocker=Yes; Interlocker Configuration=2 mm  [stored 0.00656168 ft]; Intruderprufe LowE SHGC Value=0.569; Intruderprufe LowE U Value=4.64; Intruderprufe SHGC Value=0.647; Intruderprufe U Value=6.31; Limit Sash Width Left Max=1500 mm  [stored 4.92126 ft]; Limit Sash Width Left Min=896 mm; Limit Window Width Max=2994 mm; Max Pane Area=1.49 m²; Outside Heavy Duty Interlocker=Yes; Sash Height=1407 mm  [stored 4.61614 ft]; Sash Width Left=1198 mm; Sash Width Right=1198 mm; Standard Interlocker=No; Width=2390 mm  [stored 7.84121 ft]; Windload Design=2000 mm  [stored 6.56168 ft]
- Elite-2706XX-1500Pa: Area Left Sash Glazing=0.53 m²; Area Right Sash Glazing=0.53 m²; Clearvue SHGC Value=0.547; Clearvue U Value=6.8; Custom Windload=1500 mm  [stored 4.92126 ft]; Custom Window Height=590 mm  [stored 1.9357 ft]; Custom Window Width=2690 mm; Energy Advantage SHGC Value=0.492; Energy Advantage U Value=5.54; Height=590 mm  [stored 1.9357 ft]; Inside Heavy Duty Interlocker=No; Interlocker Configuration=0 mm  [stored 0 ft]; Intruderprufe LowE SHGC Value=0.414; Intruderprufe LowE U Value=6.68; Intruderprufe SHGC Value=0.519; Intruderprufe U Value=6.69; Limit Sash Width Left Max=1500 mm  [stored 4.92126 ft]; Limit Sash Width Left Min=1196 mm; Limit Window Width Max=2994 mm; Max Pane Area=0.53 m²; Outside Heavy Duty Interlocker=No; Sash Height=507 mm; Sash Width Left=1348 mm; Sash Width Right=1348 mm; Standard Interlocker=Yes; Width=2690 mm; Windload Design=1500 mm  [stored 4.92126 ft]
- Elite-2706XX-2000Pa: Area Left Sash Glazing=0.53 m²; Area Right Sash Glazing=0.53 m²; Clearvue SHGC Value=0.547; Clearvue U Value=6.8; Custom Windload=2000 mm  [stored 6.56168 ft]; Custom Window Height=590 mm  [stored 1.9357 ft]; Custom Window Width=2690 mm; Energy Advantage SHGC Value=0.492; Energy Advantage U Value=5.54; Height=590 mm  [stored 1.9357 ft]; Inside Heavy Duty Interlocker=No; Interlocker Configuration=0 mm  [stored 0 ft]; Intruderprufe LowE SHGC Value=0.414; Intruderprufe LowE U Value=6.68; Intruderprufe SHGC Value=0.519; Intruderprufe U Value=6.69; Limit Sash Width Left Max=1500 mm  [stored 4.92126 ft]; Limit Sash Width Left Min=1196 mm; Limit Window Width Max=2994 mm; Max Pane Area=0.53 m²; Outside Heavy Duty Interlocker=No; Sash Height=507 mm; Sash Width Left=1348 mm; Sash Width Right=1348 mm; Standard Interlocker=Yes; Width=2690 mm; Windload Design=2000 mm  [stored 6.56168 ft]
- Elite-2709XX-1500Pa: Area Left Sash Glazing=0.92 m²; Area Right Sash Glazing=0.92 m²; Clearvue SHGC Value=0.626; Clearvue U Value=6.58; Custom Windload=1500 mm  [stored 4.92126 ft]; Custom Window Height=890 mm  [stored 2.91995 ft]; Custom Window Width=2690 mm; Energy Advantage SHGC Value=0.562; Energy Advantage U Value=5.09; Height=890 mm  [stored 2.91995 ft]; Inside Heavy Duty Interlocker=No; Interlocker Configuration=0 mm  [stored 0 ft]; Intruderprufe LowE SHGC Value=0.523; Intruderprufe LowE U Value=4.94; Intruderprufe SHGC Value=0.595; Intruderprufe U Value=6.46; Limit Sash Width Left Max=1500 mm  [stored 4.92126 ft]; Limit Sash Width Left Min=1196 mm; Limit Window Width Max=2994 mm; Max Pane Area=0.92 m²; Outside Heavy Duty Interlocker=No; Sash Height=807 mm  [stored 2.64764 ft]; Sash Width Left=1348 mm; Sash Width Right=1348 mm; Standard Interlocker=Yes; Width=2690 mm; Windload Design=1500 mm  [stored 4.92126 ft]
- Elite-2709XX-2000Pa: Area Left Sash Glazing=0.92 m²; Area Right Sash Glazing=0.92 m²; Clearvue SHGC Value=0.626; Clearvue U Value=6.58; Custom Windload=2000 mm  [stored 6.56168 ft]; Custom Window Height=890 mm  [stored 2.91995 ft]; Custom Window Width=2690 mm; Energy Advantage SHGC Value=0.562; Energy Advantage U Value=5.09; Height=890 mm  [stored 2.91995 ft]; Inside Heavy Duty Interlocker=No; Interlocker Configuration=0 mm  [stored 0 ft]; Intruderprufe LowE SHGC Value=0.523; Intruderprufe LowE U Value=4.94; Intruderprufe SHGC Value=0.595; Intruderprufe U Value=6.46; Limit Sash Width Left Max=1500 mm  [stored 4.92126 ft]; Limit Sash Width Left Min=1196 mm; Limit Window Width Max=2994 mm; Max Pane Area=0.92 m²; Outside Heavy Duty Interlocker=No; Sash Height=807 mm  [stored 2.64764 ft]; Sash Width Left=1348 mm; Sash Width Right=1348 mm; Standard Interlocker=Yes; Width=2690 mm; Windload Design=2000 mm  [stored 6.56168 ft]
- Elite-2712XX-1500Pa: Area Left Sash Glazing=1.31 m²; Area Right Sash Glazing=1.31 m²; Clearvue SHGC Value=0.666; Clearvue U Value=6.47; Custom Windload=1500 mm  [stored 4.92126 ft]; Custom Window Height=1190 mm  [stored 3.9042 ft]; Custom Window Width=2690 mm; Energy Advantage SHGC Value=0.597; Energy Advantage U Value=4.87; Height=1190 mm  [stored 3.9042 ft]; Inside Heavy Duty Interlocker=Yes; Interlocker Configuration=1 mm  [stored 0.00328084 ft]; Intruderprufe LowE SHGC Value=0.556; Intruderprufe LowE U Value=4.72; Intruderprufe SHGC Value=0.632; Intruderprufe U Value=6.35; Limit Sash Width Left Max=1500 mm  [stored 4.92126 ft]; Limit Sash Width Left Min=1196 mm; Limit Window Width Max=2994 mm; Max Pane Area=1.31 m²; Outside Heavy Duty Interlocker=No; Sash Height=1107 mm  [stored 3.63189 ft]; Sash Width Left=1348 mm; Sash Width Right=1348 mm; Standard Interlocker=No; Width=2690 mm; Windload Design=1500 mm  [stored 4.92126 ft]
- Elite-2712XX-2000Pa: Area Left Sash Glazing=1.31 m²; Area Right Sash Glazing=1.31 m²; Clearvue SHGC Value=0.666; Clearvue U Value=6.47; Custom Windload=2000 mm  [stored 6.56168 ft]; Custom Window Height=1190 mm  [stored 3.9042 ft]; Custom Window Width=2690 mm; Energy Advantage SHGC Value=0.597; Energy Advantage U Value=4.87; Height=1190 mm  [stored 3.9042 ft]; Inside Heavy Duty Interlocker=Yes; Interlocker Configuration=1 mm  [stored 0.00328084 ft]; Intruderprufe LowE SHGC Value=0.556; Intruderprufe LowE U Value=4.72; Intruderprufe SHGC Value=0.632; Intruderprufe U Value=6.35; Limit Sash Width Left Max=1500 mm  [stored 4.92126 ft]; Limit Sash Width Left Min=1196 mm; Limit Window Width Max=2994 mm; Max Pane Area=1.31 m²; Outside Heavy Duty Interlocker=No; Sash Height=1107 mm  [stored 3.63189 ft]; Sash Width Left=1348 mm; Sash Width Right=1348 mm; Standard Interlocker=No; Width=2690 mm; Windload Design=2000 mm  [stored 6.56168 ft]
- Elite-2715XX-1500Pa: Area Left Sash Glazing=1.69 m²; Area Right Sash Glazing=1.69 m²; Clearvue SHGC Value=0.69; Clearvue U Value=6.4; Custom Windload=1500 mm  [stored 4.92126 ft]; Custom Window Height=1490 mm  [stored 4.88845 ft]; Custom Window Width=2690 mm; Energy Advantage SHGC Value=0.618; Energy Advantage U Value=4.74; Height=1490 mm  [stored 4.88845 ft]; Inside Heavy Duty Interlocker=Yes; Interlocker Configuration=2 mm  [stored 0.00656168 ft]; Intruderprufe LowE SHGC Value=0.575; Intruderprufe LowE U Value=4.59; Intruderprufe SHGC Value=0.654; Intruderprufe U Value=6.28; Limit Sash Width Left Max=1500 mm  [stored 4.92126 ft]; Limit Sash Width Left Min=1196 mm; Limit Window Width Max=2994 mm; Max Pane Area=1.69 m²; Outside Heavy Duty Interlocker=Yes; Sash Height=1407 mm  [stored 4.61614 ft]; Sash Width Left=1348 mm; Sash Width Right=1348 mm; Standard Interlocker=No; Width=2690 mm; Windload Design=1500 mm  [stored 4.92126 ft]
- Elite-2715XX-2000Pa: Area Left Sash Glazing=1.69 m²; Area Right Sash Glazing=1.69 m²; Clearvue SHGC Value=0.69; Clearvue U Value=6.4; Custom Windload=2000 mm  [stored 6.56168 ft]; Custom Window Height=1490 mm  [stored 4.88845 ft]; Custom Window Width=2690 mm; Energy Advantage SHGC Value=0.618; Energy Advantage U Value=4.74; Height=1490 mm  [stored 4.88845 ft]; Inside Heavy Duty Interlocker=Yes; Interlocker Configuration=2 mm  [stored 0.00656168 ft]; Intruderprufe LowE SHGC Value=0.575; Intruderprufe LowE U Value=4.59; Intruderprufe SHGC Value=0.654; Intruderprufe U Value=6.28; Limit Sash Width Left Max=1500 mm  [stored 4.92126 ft]; Limit Sash Width Left Min=1196 mm; Limit Window Width Max=2994 mm; Max Pane Area=1.69 m²; Outside Heavy Duty Interlocker=Yes; Sash Height=1407 mm  [stored 4.61614 ft]; Sash Width Left=1348 mm; Sash Width Right=1348 mm; Standard Interlocker=No; Width=2690 mm; Windload Design=2000 mm  [stored 6.56168 ft]
- Elite-3006XX-1500Pa: Area Left Sash Glazing=0.6 m²; Area Right Sash Glazing=0.6 m²; Clearvue SHGC Value=0.551; Clearvue U Value=6.79; Custom Windload=1500 mm  [stored 4.92126 ft]; Custom Window Height=590 mm  [stored 1.9357 ft]; Custom Window Width=2990 mm; Energy Advantage SHGC Value=0.495; Energy Advantage U Value=5.5; Height=590 mm  [stored 1.9357 ft]; Inside Heavy Duty Interlocker=No; Interlocker Configuration=0 mm  [stored 0 ft]; Intruderprufe LowE SHGC Value=0.462; Intruderprufe LowE U Value=5.36; Intruderprufe SHGC Value=0.524; Intruderprufe U Value=6.67; Limit Sash Width Left Max=1500 mm  [stored 4.92126 ft]; Limit Sash Width Left Min=1496 mm; Limit Window Width Max=2994 mm; Max Pane Area=0.6 m²; Outside Heavy Duty Interlocker=No; Sash Height=507 mm; Sash Width Left=1498 mm; Sash Width Right=1498 mm; Standard Interlocker=Yes; Width=2990 mm; Windload Design=1500 mm  [stored 4.92126 ft]
- Elite-3006XX-2000Pa: Area Left Sash Glazing=0.6 m²; Area Right Sash Glazing=0.6 m²; Clearvue SHGC Value=0.551; Clearvue U Value=6.79; Custom Windload=2000 mm  [stored 6.56168 ft]; Custom Window Height=590 mm  [stored 1.9357 ft]; Custom Window Width=2990 mm; Energy Advantage SHGC Value=0.495; Energy Advantage U Value=5.5; Height=590 mm  [stored 1.9357 ft]; Inside Heavy Duty Interlocker=No; Interlocker Configuration=0 mm  [stored 0 ft]; Intruderprufe LowE SHGC Value=0.462; Intruderprufe LowE U Value=5.36; Intruderprufe SHGC Value=0.524; Intruderprufe U Value=6.67; Limit Sash Width Left Max=1500 mm  [stored 4.92126 ft]; Limit Sash Width Left Min=1496 mm; Limit Window Width Max=2994 mm; Max Pane Area=0.6 m²; Outside Heavy Duty Interlocker=No; Sash Height=507 mm; Sash Width Left=1498 mm; Sash Width Right=1498 mm; Standard Interlocker=Yes; Width=2990 mm; Windload Design=2000 mm  [stored 6.56168 ft]
- Elite-3009XX-1500Pa: Area Left Sash Glazing=1.03 m²; Area Right Sash Glazing=1.03 m²; Clearvue SHGC Value=0.632; Clearvue U Value=6.56; Custom Windload=1500 mm  [stored 4.92126 ft]; Custom Window Height=890 mm  [stored 2.91995 ft]; Custom Window Width=2990 mm; Energy Advantage SHGC Value=0.567; Energy Advantage U Value=5.05; Height=890 mm  [stored 2.91995 ft]; Inside Heavy Duty Interlocker=No; Interlocker Configuration=0 mm  [stored 0 ft]; Intruderprufe LowE SHGC Value=0.528; Intruderprufe LowE U Value=4.91; Intruderprufe SHGC Value=0.6; Intruderprufe U Value=6.44; Limit Sash Width Left Max=1500 mm  [stored 4.92126 ft]; Limit Sash Width Left Min=1496 mm; Limit Window Width Max=2994 mm; Max Pane Area=1.03 m²; Outside Heavy Duty Interlocker=No; Sash Height=807 mm  [stored 2.64764 ft]; Sash Width Left=1498 mm; Sash Width Right=1498 mm; Standard Interlocker=Yes; Width=2990 mm; Windload Design=1500 mm  [stored 4.92126 ft]
- Elite-3009XX-2000Pa: Area Left Sash Glazing=1.03 m²; Area Right Sash Glazing=1.03 m²; Clearvue SHGC Value=0.632; Clearvue U Value=6.56; Custom Windload=2000 mm  [stored 6.56168 ft]; Custom Window Height=890 mm  [stored 2.91995 ft]; Custom Window Width=2990 mm; Energy Advantage SHGC Value=0.567; Energy Advantage U Value=5.05; Height=890 mm  [stored 2.91995 ft]; Inside Heavy Duty Interlocker=No; Interlocker Configuration=0 mm  [stored 0 ft]; Intruderprufe LowE SHGC Value=0.528; Intruderprufe LowE U Value=4.91; Intruderprufe SHGC Value=0.6; Intruderprufe U Value=6.44; Limit Sash Width Left Max=1500 mm  [stored 4.92126 ft]; Limit Sash Width Left Min=1496 mm; Limit Window Width Max=2994 mm; Max Pane Area=1.03 m²; Outside Heavy Duty Interlocker=No; Sash Height=807 mm  [stored 2.64764 ft]; Sash Width Left=1498 mm; Sash Width Right=1498 mm; Standard Interlocker=Yes; Width=2990 mm; Windload Design=2000 mm  [stored 6.56168 ft]
- Elite-3012XX-1500Pa: Area Left Sash Glazing=1.46 m²; Area Right Sash Glazing=1.46 m²; Clearvue SHGC Value=0.672; Clearvue U Value=6.45; Custom Windload=1500 mm  [stored 4.92126 ft]; Custom Window Height=1190 mm  [stored 3.9042 ft]; Custom Window Width=2990 mm; Energy Advantage SHGC Value=0.602; Energy Advantage U Value=4.83; Height=1190 mm  [stored 3.9042 ft]; Inside Heavy Duty Interlocker=Yes; Interlocker Configuration=1 mm  [stored 0.00328084 ft]; Intruderprufe LowE SHGC Value=0.56; Intruderprufe LowE U Value=4.69; Intruderprufe SHGC Value=0.637; Intruderprufe U Value=6.32; Limit Sash Width Left Max=1500 mm  [stored 4.92126 ft]; Limit Sash Width Left Min=1496 mm; Limit Window Width Max=2994 mm; Max Pane Area=1.46 m²; Outside Heavy Duty Interlocker=No; Sash Height=1107 mm  [stored 3.63189 ft]; Sash Width Left=1498 mm; Sash Width Right=1498 mm; Standard Interlocker=No; Width=2990 mm; Windload Design=1500 mm  [stored 4.92126 ft]
- Elite-3012XX-2000Pa: Area Left Sash Glazing=1.46 m²; Area Right Sash Glazing=1.46 m²; Clearvue SHGC Value=0.672; Clearvue U Value=6.45; Custom Windload=2000 mm  [stored 6.56168 ft]; Custom Window Height=1190 mm  [stored 3.9042 ft]; Custom Window Width=2990 mm; Energy Advantage SHGC Value=0.602; Energy Advantage U Value=4.83; Height=1190 mm  [stored 3.9042 ft]; Inside Heavy Duty Interlocker=Yes; Interlocker Configuration=1 mm  [stored 0.00328084 ft]; Intruderprufe LowE SHGC Value=0.56; Intruderprufe LowE U Value=4.69; Intruderprufe SHGC Value=0.637; Intruderprufe U Value=6.32; Limit Sash Width Left Max=1500 mm  [stored 4.92126 ft]; Limit Sash Width Left Min=1496 mm; Limit Window Width Max=2994 mm; Max Pane Area=1.46 m²; Outside Heavy Duty Interlocker=No; Sash Height=1107 mm  [stored 3.63189 ft]; Sash Width Left=1498 mm; Sash Width Right=1498 mm; Standard Interlocker=No; Width=2990 mm; Windload Design=2000 mm  [stored 6.56168 ft]
- Elite-3015XX-1500Pa: Area Left Sash Glazing=1.89 m²; Area Right Sash Glazing=1.89 m²; Clearvue SHGC Value=0.695; Clearvue U Value=6.38; Custom Windload=1500 mm  [stored 4.92126 ft]; Custom Window Height=1490 mm  [stored 4.88845 ft]; Custom Window Width=2990 mm; Energy Advantage SHGC Value=0.623; Energy Advantage U Value=4.69; Height=1490 mm  [stored 4.88845 ft]; Inside Heavy Duty Interlocker=Yes; Interlocker Configuration=2 mm  [stored 0.00656168 ft]; Intruderprufe LowE SHGC Value=0.579; Intruderprufe LowE U Value=4.56; Intruderprufe SHGC Value=0.66; Intruderprufe U Value=6.26; Limit Sash Width Left Max=1500 mm  [stored 4.92126 ft]; Limit Sash Width Left Min=1496 mm; Limit Window Width Max=2994 mm; Max Pane Area=1.89 m²; Outside Heavy Duty Interlocker=Yes; Sash Height=1407 mm  [stored 4.61614 ft]; Sash Width Left=1498 mm; Sash Width Right=1498 mm; Standard Interlocker=No; Width=2990 mm; Windload Design=1500 mm  [stored 4.92126 ft]
- Elite-3015XX-2000Pa: Area Left Sash Glazing=1.89 m²; Area Right Sash Glazing=1.89 m²; Clearvue SHGC Value=0.695; Clearvue U Value=6.38; Custom Windload=2000 mm  [stored 6.56168 ft]; Custom Window Height=1490 mm  [stored 4.88845 ft]; Custom Window Width=2990 mm; Energy Advantage SHGC Value=0.623; Energy Advantage U Value=4.69; Height=1490 mm  [stored 4.88845 ft]; Inside Heavy Duty Interlocker=Yes; Interlocker Configuration=2 mm  [stored 0.00656168 ft]; Intruderprufe LowE SHGC Value=0.579; Intruderprufe LowE U Value=4.56; Intruderprufe SHGC Value=0.66; Intruderprufe U Value=6.26; Limit Sash Width Left Max=1500 mm  [stored 4.92126 ft]; Limit Sash Width Left Min=1496 mm; Limit Window Width Max=2994 mm; Max Pane Area=1.89 m²; Outside Heavy Duty Interlocker=Yes; Sash Height=1407 mm  [stored 4.61614 ft]; Sash Width Left=1498 mm; Sash Width Right=1498 mm; Standard Interlocker=No; Width=2990 mm; Windload Design=2000 mm  [stored 6.56168 ft]

note: [stored X ft] marks values corroborated as IEEE doubles in the binary element streams (Revit-internal decimal feet)

## geometry (parser evidence)
native form markers: Sweep x49
no freeform markers — native parametric forms only
